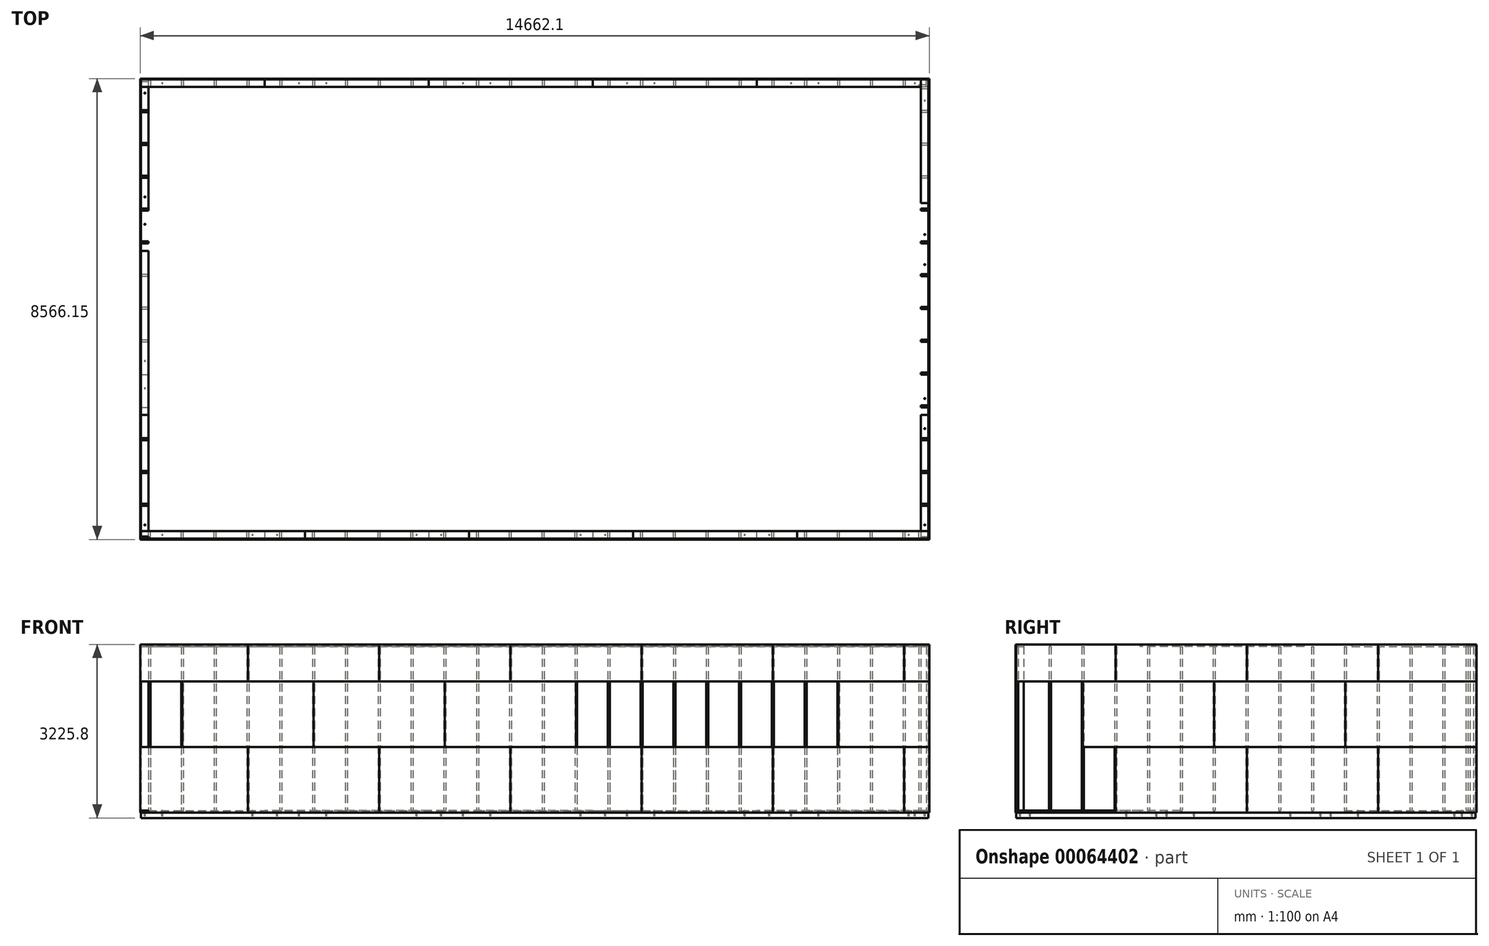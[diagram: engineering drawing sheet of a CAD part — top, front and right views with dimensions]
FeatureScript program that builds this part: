
annotation { "Feature Type Name" : "Feature", "Feature Type Description" : "" }
export const myFeature = defineFeature(function(context is Context, id is Id, definition is map)
    precondition{}
    {
        {
            var Q0;
            Q0=qCreatedBy(makeId("Top.planeOp"),FACE);
            var sketch = newSketch(context, id + "F0", { "sketchPlane" : qUnion([Q0])});
            skLineSegment(sketch, "E0.bottom", {"start": v(0, 8534.4) * mm, "end": v(14630.4, 8534.4) * mm});
            skLineSegment(sketch, "E0.top", {"start": v(0, 0) * mm, "end": v(14630.4, 0) * mm});
            skLineSegment(sketch, "E0.left", {"start": v(0, 8534.4) * mm, "end": v(0, 0) * mm});
            skLineSegment(sketch, "E0.right", {"start": v(14630.4, 8534.4) * mm, "end": v(14630.4, 0) * mm});
            skSolve(sketch);
        }
        {
            var Q0;
            Q0=makeQuery(id+"F0.imprint","IMPRINT",FACE,{"disambiguationData":[TD([[makeQuery(id+"F0.imprint","IMPRINT",EDGE,{"derivedFrom":sQuery(id+"F0.wireOp",EDGE,"E0.bottom")}),-1.0]])]});
            extrude(context, id + "F1", {"entities" : qUnion([Q0]), "oppositeDirection" : true, "depth" : 101.6 * mm});
        }
        {
            var Q0;
            Q0=makeQuery(id+"F1.opExtrude","CAP_FACE",FACE,{"disambiguationData":[OSD([sQuery(id+"F0.wireOp",EDGE,"E0.bottom"),sQuery(id+"F0.wireOp",EDGE,"E0.top"),sQuery(id+"F0.wireOp",EDGE,"E0.left"),sQuery(id+"F0.wireOp",EDGE,"E0.right")])],"isStart":true});
            var sketch = newSketch(context, id + "F2", { "sketchPlane" : qUnion([Q0])});
            skLineSegment(sketch, "E1.bottom", {"start": v(0, 0) * mm, "end": v(139.7, 0) * mm});
            skLineSegment(sketch, "E1.top", {"start": v(0, 3048) * mm, "end": v(139.7, 3048) * mm});
            skLineSegment(sketch, "E1.left", {"start": v(0, 0) * mm, "end": v(0, 3048) * mm});
            skLineSegment(sketch, "E1.right", {"start": v(139.7, 0) * mm, "end": v(139.7, 3048) * mm});
            skLineSegment(sketch, "E2.bottom", {"start": v(139.7, 8534.4) * mm, "end": v(3187.7, 8534.4) * mm});
            skLineSegment(sketch, "E2.top", {"start": v(139.7, 8394.7) * mm, "end": v(3187.7, 8394.7) * mm});
            skLineSegment(sketch, "E2.left", {"start": v(139.7, 8534.4) * mm, "end": v(139.7, 8394.7) * mm});
            skLineSegment(sketch, "E2.right", {"start": v(3187.7, 8534.4) * mm, "end": v(3187.7, 8394.7) * mm});
            skLineSegment(sketch, "E3.bottom", {"start": v(3187.7, 8394.7) * mm, "end": v(6235.7, 8394.7) * mm});
            skLineSegment(sketch, "E3.top", {"start": v(3187.7, 8534.4) * mm, "end": v(6235.7, 8534.4) * mm});
            skLineSegment(sketch, "E3.left", {"start": v(3187.7, 8394.7) * mm, "end": v(3187.7, 8534.4) * mm});
            skLineSegment(sketch, "E3.right", {"start": v(6235.7, 8394.7) * mm, "end": v(6235.7, 8534.4) * mm});
            skLineSegment(sketch, "E4.bottom", {"start": v(6235.7, 8394.7) * mm, "end": v(9283.7, 8394.7) * mm});
            skLineSegment(sketch, "E4.top", {"start": v(6235.7, 8534.4) * mm, "end": v(9283.7, 8534.4) * mm});
            skLineSegment(sketch, "E4.right", {"start": v(9283.7, 8394.7) * mm, "end": v(9283.7, 8534.4) * mm});
            skLineSegment(sketch, "E5.bottom", {"start": v(9283.7, 8394.7) * mm, "end": v(12331.7, 8394.7) * mm});
            skLineSegment(sketch, "E5.top", {"start": v(9283.7, 8534.4) * mm, "end": v(12331.7, 8534.4) * mm});
            skLineSegment(sketch, "E5.right", {"start": v(12331.7, 8394.7) * mm, "end": v(12331.7, 8534.4) * mm});
            skLineSegment(sketch, "E6.bottom", {"start": v(12331.7, 8394.7) * mm, "end": v(14630.4, 8394.7) * mm});
            skLineSegment(sketch, "E6.top", {"start": v(12331.7, 8534.4) * mm, "end": v(14630.4, 8534.4) * mm});
            skLineSegment(sketch, "E6.right", {"start": v(14630.4, 8394.7) * mm, "end": v(14630.4, 8534.4) * mm});
            skLineSegment(sketch, "E7.bottom", {"start": v(139.7, 3048) * mm, "end": v(0, 3048) * mm});
            skLineSegment(sketch, "E7.top", {"start": v(139.7, 6096) * mm, "end": v(0, 6096) * mm});
            skLineSegment(sketch, "E7.left", {"start": v(139.7, 3048) * mm, "end": v(139.7, 6096) * mm});
            skLineSegment(sketch, "E7.right", {"start": v(0, 3048) * mm, "end": v(0, 6096) * mm});
            skLineSegment(sketch, "E8.top", {"start": v(139.7, 8534.4) * mm, "end": v(0, 8534.4) * mm});
            skLineSegment(sketch, "E8.left", {"start": v(139.7, 6096) * mm, "end": v(139.7, 8534.4) * mm});
            skLineSegment(sketch, "E8.right", {"start": v(0, 6096) * mm, "end": v(0, 8534.4) * mm});
            skLineSegment(sketch, "E9.bottom", {"start": v(14630.4, 8394.7) * mm, "end": v(14490.7, 8394.7) * mm});
            skLineSegment(sketch, "E9.top", {"start": v(14630.4, 5346.7) * mm, "end": v(14490.7, 5346.7) * mm});
            skLineSegment(sketch, "E9.left", {"start": v(14630.4, 8394.7) * mm, "end": v(14630.4, 5346.7) * mm});
            skLineSegment(sketch, "E9.right", {"start": v(14490.7, 8394.7) * mm, "end": v(14490.7, 5346.7) * mm});
            skLineSegment(sketch, "E10.bottom", {"start": v(14490.7, 5346.7) * mm, "end": v(14630.4, 5346.7) * mm});
            skLineSegment(sketch, "E10.top", {"start": v(14490.7, 2298.7) * mm, "end": v(14630.4, 2298.7) * mm});
            skLineSegment(sketch, "E10.left", {"start": v(14490.7, 5346.7) * mm, "end": v(14490.7, 2298.7) * mm});
            skLineSegment(sketch, "E10.right", {"start": v(14630.4, 5346.7) * mm, "end": v(14630.4, 2298.7) * mm});
            skLineSegment(sketch, "E11.top", {"start": v(14490.7, 0) * mm, "end": v(14630.4, 0) * mm});
            skLineSegment(sketch, "E11.left", {"start": v(14490.7, 2298.7) * mm, "end": v(14490.7, 0) * mm});
            skLineSegment(sketch, "E11.right", {"start": v(14630.4, 2298.7) * mm, "end": v(14630.4, 0) * mm});
            skLineSegment(sketch, "E12.bottom", {"start": v(14490.7, 0) * mm, "end": v(11442.7, 0) * mm});
            skLineSegment(sketch, "E12.top", {"start": v(14490.7, 139.7) * mm, "end": v(11442.7, 139.7) * mm});
            skLineSegment(sketch, "E12.left", {"start": v(14490.7, 0) * mm, "end": v(14490.7, 139.7) * mm});
            skLineSegment(sketch, "E12.right", {"start": v(11442.7, 0) * mm, "end": v(11442.7, 139.7) * mm});
            skLineSegment(sketch, "E13.bottom", {"start": v(11442.7, 139.7) * mm, "end": v(8394.7, 139.7) * mm});
            skLineSegment(sketch, "E13.top", {"start": v(11442.7, 0) * mm, "end": v(8394.7, 0) * mm});
            skLineSegment(sketch, "E13.left", {"start": v(11442.7, 139.7) * mm, "end": v(11442.7, 0) * mm});
            skLineSegment(sketch, "E13.right", {"start": v(8394.7, 139.7) * mm, "end": v(8394.7, 0) * mm});
            skLineSegment(sketch, "E14.bottom", {"start": v(8394.7, 139.7) * mm, "end": v(5346.7, 139.7) * mm});
            skLineSegment(sketch, "E14.top", {"start": v(8394.7, 0) * mm, "end": v(5346.7, 0) * mm});
            skLineSegment(sketch, "E14.right", {"start": v(5346.7, 139.7) * mm, "end": v(5346.7, 0) * mm});
            skLineSegment(sketch, "E15.bottom", {"start": v(5346.7, 139.7) * mm, "end": v(2298.7, 139.7) * mm});
            skLineSegment(sketch, "E15.top", {"start": v(5346.7, 0) * mm, "end": v(2298.7, 0) * mm});
            skLineSegment(sketch, "E15.right", {"start": v(2298.7, 139.7) * mm, "end": v(2298.7, 0) * mm});
            skLineSegment(sketch, "E16.bottom", {"start": v(2298.7, 139.7) * mm, "end": v(139.7, 139.7) * mm});
            skLineSegment(sketch, "E16.top", {"start": v(2298.7, 0) * mm, "end": v(139.7, 0) * mm});
            skLineSegment(sketch, "E16.right", {"start": v(139.7, 139.7) * mm, "end": v(139.7, 0) * mm});
            skSolve(sketch);
        }
        {
            var Q0;
            Q0=makeQuery(id+"F2.imprint","IMPRINT",FACE,{"disambiguationData":[TD([[makeQuery(id+"F2.imprint","IMPRINT",EDGE,{"derivedFrom":sQuery(id+"F2.wireOp",EDGE,"E1.bottom")}),1.0]])]});
            var Q1;
            {var subQ3=sQuery(id+"F2.wireOp",EDGE,"E7.top");Q1=makeQuery(id+"F2.imprint","IMPRINT",FACE,{"disambiguationData":[TD([[makeQuery(id+"F2.imprint","IMPRINT",EDGE,{"derivedFrom":subQ3}),-1.0]])]});}
            var Q2;
            Q2=makeQuery(id+"F2.imprint","IMPRINT",FACE,{"disambiguationData":[TD([[makeQuery(id+"F2.imprint","IMPRINT",EDGE,{"derivedFrom":sQuery(id+"F2.wireOp",EDGE,"E3.bottom")}),1.0]])]});
            var Q3;
            Q3=makeQuery(id+"F2.imprint","IMPRINT",FACE,{"disambiguationData":[TD([[makeQuery(id+"F2.imprint","IMPRINT",EDGE,{"derivedFrom":sQuery(id+"F2.wireOp",EDGE,"E5.bottom")}),1.0]])]});
            var Q4;
            Q4=makeQuery(id+"F2.imprint","IMPRINT",FACE,{"disambiguationData":[TD([[makeQuery(id+"F2.imprint","IMPRINT",EDGE,{"derivedFrom":sQuery(id+"F2.wireOp",EDGE,"E9.bottom")}),1.0]])]});
            var Q5;
            Q5=makeQuery(id+"F2.imprint","IMPRINT",FACE,{"disambiguationData":[TD([[makeQuery(id+"F2.imprint","IMPRINT",EDGE,{"derivedFrom":sQuery(id+"F2.wireOp",EDGE,"E10.top")}),-1.0]])]});
            var Q6;
            Q6=makeQuery(id+"F2.imprint","IMPRINT",FACE,{"disambiguationData":[TD([[makeQuery(id+"F2.imprint","IMPRINT",EDGE,{"derivedFrom":sQuery(id+"F2.wireOp",EDGE,"E13.bottom")}),1.0]])]});
            var Q7;
            Q7=makeQuery(id+"F2.imprint","IMPRINT",FACE,{"disambiguationData":[TD([[makeQuery(id+"F2.imprint","IMPRINT",EDGE,{"derivedFrom":sQuery(id+"F2.wireOp",EDGE,"E15.bottom")}),1.0]])]});
            extrude(context, id + "F3", {"entities" : qUnion([Q0, Q1, Q2, Q3, Q4, Q5, Q6, Q7]), "depth" : 38.1 * mm});
        }
        {
            var Q0;
            Q0=makeQuery(id+"F2.imprint","IMPRINT",FACE,{"disambiguationData":[TD([[makeQuery(id+"F2.imprint","IMPRINT",EDGE,{"derivedFrom":sQuery(id+"F2.wireOp",EDGE,"E7.bottom")}),-1.0]])]});
            var Q1;
            {var subQ0=sQuery(id+"F2.wireOp",EDGE,"E2.bottom");Q1=makeQuery(id+"F2.imprint","IMPRINT",FACE,{"disambiguationData":[TD([[makeQuery(id+"F2.imprint","IMPRINT",EDGE,{"derivedFrom":subQ0}),-1.0]])]});}
            var Q2;
            Q2=makeQuery(id+"F2.imprint","IMPRINT",FACE,{"disambiguationData":[TD([[makeQuery(id+"F2.imprint","IMPRINT",EDGE,{"derivedFrom":sQuery(id+"F2.wireOp",EDGE,"E4.bottom")}),1.0]])]});
            var Q3;
            Q3=makeQuery(id+"F2.imprint","IMPRINT",FACE,{"disambiguationData":[TD([[makeQuery(id+"F2.imprint","IMPRINT",EDGE,{"derivedFrom":sQuery(id+"F2.wireOp",EDGE,"E6.bottom")}),1.0]])]});
            var Q4;
            Q4=makeQuery(id+"F2.imprint","IMPRINT",FACE,{"disambiguationData":[TD([[makeQuery(id+"F2.imprint","IMPRINT",EDGE,{"derivedFrom":sQuery(id+"F2.wireOp",EDGE,"E10.bottom")}),-1.0]])]});
            var Q5;
            Q5=makeQuery(id+"F2.imprint","IMPRINT",FACE,{"disambiguationData":[TD([[makeQuery(id+"F2.imprint","IMPRINT",EDGE,{"derivedFrom":sQuery(id+"F2.wireOp",EDGE,"E12.bottom")}),1.0]])]});
            var Q6;
            Q6=makeQuery(id+"F2.imprint","IMPRINT",FACE,{"disambiguationData":[TD([[makeQuery(id+"F2.imprint","IMPRINT",EDGE,{"derivedFrom":sQuery(id+"F2.wireOp",EDGE,"E14.bottom")}),1.0]])]});
            var Q7;
            Q7=makeQuery(id+"F2.imprint","IMPRINT",FACE,{"disambiguationData":[TD([[makeQuery(id+"F2.imprint","IMPRINT",EDGE,{"derivedFrom":sQuery(id+"F2.wireOp",EDGE,"E16.bottom")}),1.0]])]});
            extrude(context, id + "F4", {"entities" : qUnion([Q0, Q1, Q2, Q3, Q4, Q5, Q6, Q7]), "depth" : 38.1 * mm});
        }
        {
            var Q0;
            Q0=makeQuery(id+"F3.opExtrude","CAP_FACE",FACE,{"disambiguationData":[OSD([sQuery(id+"F2.wireOp",EDGE,"E1.bottom"),sQuery(id+"F2.wireOp",EDGE,"E1.left"),sQuery(id+"F2.wireOp",EDGE,"E1.right"),sQuery(id+"F2.wireOp",EDGE,"E7.bottom"),sQuery(id+"F2.wireOp",EDGE,"E16.right")])],"isStart":false});
            var sketch = newSketch(context, id + "F5", { "sketchPlane" : qUnion([Q0])});
            skLineSegment(sketch, "E17.bottom", {"start": v(0, 0) * mm, "end": v(139.7, 0) * mm});
            skLineSegment(sketch, "E17.top", {"start": v(0, 38.1) * mm, "end": v(139.7, 38.1) * mm});
            skLineSegment(sketch, "E17.left", {"start": v(0, 0) * mm, "end": v(0, 38.1) * mm});
            skLineSegment(sketch, "E17.right", {"start": v(139.7, 0) * mm, "end": v(139.7, 38.1) * mm});
            skLineSegment(sketch, "E18.bottom", {"start": v(139.7, 38.1) * mm, "end": v(101.6, 38.1) * mm});
            skLineSegment(sketch, "E18.top", {"start": v(139.7, 177.8) * mm, "end": v(101.6, 177.8) * mm});
            skLineSegment(sketch, "E18.left", {"start": v(139.7, 38.1) * mm, "end": v(139.7, 177.8) * mm});
            skLineSegment(sketch, "E18.right", {"start": v(101.6, 38.1) * mm, "end": v(101.6, 177.8) * mm});
            skLineSegment(sketch, "E19.0", {"start": v(2298.7, 139.7) * mm, "end": v(139.7, 139.7) * mm, "construction": true});
            skLineSegment(sketch, "E20.bottom", {"start": v(139.7, 0) * mm, "end": v(177.8, 0) * mm});
            skLineSegment(sketch, "E20.top", {"start": v(139.7, 139.7) * mm, "end": v(177.8, 139.7) * mm});
            skLineSegment(sketch, "E20.left", {"start": v(139.7, 0) * mm, "end": v(139.7, 139.7) * mm});
            skLineSegment(sketch, "E20.right", {"start": v(177.8, 0) * mm, "end": v(177.8, 139.7) * mm});
            skLineSegment(sketch, "E21.1.0.0", {"start": v(749.3, 0) * mm, "end": v(749.3, 139.7) * mm});
            skLineSegment(sketch, "E21.1.0.1", {"start": v(749.3, 139.7) * mm, "end": v(787.4, 139.7) * mm});
            skLineSegment(sketch, "E21.1.0.2", {"start": v(787.4, 0) * mm, "end": v(787.4, 139.7) * mm});
            skLineSegment(sketch, "E21.1.0.3", {"start": v(749.3, 0) * mm, "end": v(787.4, 0) * mm});
            skLineSegment(sketch, "E21.2.0.0", {"start": v(1358.9, 0) * mm, "end": v(1358.9, 139.7) * mm});
            skLineSegment(sketch, "E21.2.0.1", {"start": v(1358.9, 139.7) * mm, "end": v(1397, 139.7) * mm});
            skLineSegment(sketch, "E21.2.0.2", {"start": v(1397, 0) * mm, "end": v(1397, 139.7) * mm});
            skLineSegment(sketch, "E21.2.0.3", {"start": v(1358.9, 0) * mm, "end": v(1397, 0) * mm});
            skLineSegment(sketch, "E21.3.0.0", {"start": v(1968.5, 0) * mm, "end": v(1968.5, 139.7) * mm});
            skLineSegment(sketch, "E21.3.0.1", {"start": v(1968.5, 139.7) * mm, "end": v(2006.6, 139.7) * mm});
            skLineSegment(sketch, "E21.3.0.2", {"start": v(2006.6, 0) * mm, "end": v(2006.6, 139.7) * mm});
            skLineSegment(sketch, "E21.3.0.3", {"start": v(1968.5, 0) * mm, "end": v(2006.6, 0) * mm});
            skLineSegment(sketch, "E21.4.0.0", {"start": v(2578.1, 0) * mm, "end": v(2578.1, 139.7) * mm});
            skLineSegment(sketch, "E21.4.0.1", {"start": v(2578.1, 139.7) * mm, "end": v(2616.2, 139.7) * mm});
            skLineSegment(sketch, "E21.4.0.2", {"start": v(2616.2, 0) * mm, "end": v(2616.2, 139.7) * mm});
            skLineSegment(sketch, "E21.4.0.3", {"start": v(2578.1, 0) * mm, "end": v(2616.2, 0) * mm});
            skLineSegment(sketch, "E21.5.0.0", {"start": v(3187.7, 0) * mm, "end": v(3187.7, 139.7) * mm});
            skLineSegment(sketch, "E21.5.0.1", {"start": v(3187.7, 139.7) * mm, "end": v(3225.8, 139.7) * mm});
            skLineSegment(sketch, "E21.5.0.2", {"start": v(3225.8, 0) * mm, "end": v(3225.8, 139.7) * mm});
            skLineSegment(sketch, "E21.5.0.3", {"start": v(3187.7, 0) * mm, "end": v(3225.8, 0) * mm});
            skLineSegment(sketch, "E21.6.0.0", {"start": v(3797.3, 0) * mm, "end": v(3797.3, 139.7) * mm});
            skLineSegment(sketch, "E21.6.0.1", {"start": v(3797.3, 139.7) * mm, "end": v(3835.4, 139.7) * mm});
            skLineSegment(sketch, "E21.6.0.2", {"start": v(3835.4, 0) * mm, "end": v(3835.4, 139.7) * mm});
            skLineSegment(sketch, "E21.6.0.3", {"start": v(3797.3, 0) * mm, "end": v(3835.4, 0) * mm});
            skLineSegment(sketch, "E21.7.0.0", {"start": v(4406.9, 0) * mm, "end": v(4406.9, 139.7) * mm});
            skLineSegment(sketch, "E21.7.0.1", {"start": v(4406.9, 139.7) * mm, "end": v(4445, 139.7) * mm});
            skLineSegment(sketch, "E21.7.0.2", {"start": v(4445, 0) * mm, "end": v(4445, 139.7) * mm});
            skLineSegment(sketch, "E21.7.0.3", {"start": v(4406.9, 0) * mm, "end": v(4445, 0) * mm});
            skLineSegment(sketch, "E21.8.0.0", {"start": v(5016.5, 0) * mm, "end": v(5016.5, 139.7) * mm});
            skLineSegment(sketch, "E21.8.0.1", {"start": v(5016.5, 139.7) * mm, "end": v(5054.6, 139.7) * mm});
            skLineSegment(sketch, "E21.8.0.2", {"start": v(5054.6, 0) * mm, "end": v(5054.6, 139.7) * mm});
            skLineSegment(sketch, "E21.8.0.3", {"start": v(5016.5, 0) * mm, "end": v(5054.6, 0) * mm});
            skLineSegment(sketch, "E21.9.0.0", {"start": v(5626.1, 0) * mm, "end": v(5626.1, 139.7) * mm});
            skLineSegment(sketch, "E21.9.0.1", {"start": v(5626.1, 139.7) * mm, "end": v(5664.2, 139.7) * mm});
            skLineSegment(sketch, "E21.9.0.2", {"start": v(5664.2, 0) * mm, "end": v(5664.2, 139.7) * mm});
            skLineSegment(sketch, "E21.9.0.3", {"start": v(5626.1, 0) * mm, "end": v(5664.2, 0) * mm});
            skLineSegment(sketch, "E21.10.0.0", {"start": v(6235.7, 0) * mm, "end": v(6235.7, 139.7) * mm});
            skLineSegment(sketch, "E21.10.0.1", {"start": v(6235.7, 139.7) * mm, "end": v(6273.8, 139.7) * mm});
            skLineSegment(sketch, "E21.10.0.2", {"start": v(6273.8, 0) * mm, "end": v(6273.8, 139.7) * mm});
            skLineSegment(sketch, "E21.10.0.3", {"start": v(6235.7, 0) * mm, "end": v(6273.8, 0) * mm});
            skLineSegment(sketch, "E21.11.0.0", {"start": v(6845.3, 0) * mm, "end": v(6845.3, 139.7) * mm});
            skLineSegment(sketch, "E21.11.0.1", {"start": v(6845.3, 139.7) * mm, "end": v(6883.4, 139.7) * mm});
            skLineSegment(sketch, "E21.11.0.2", {"start": v(6883.4, 0) * mm, "end": v(6883.4, 139.7) * mm});
            skLineSegment(sketch, "E21.11.0.3", {"start": v(6845.3, 0) * mm, "end": v(6883.4, 0) * mm});
            skLineSegment(sketch, "E21.12.0.0", {"start": v(7454.9, 0) * mm, "end": v(7454.9, 139.7) * mm});
            skLineSegment(sketch, "E21.12.0.1", {"start": v(7454.9, 139.7) * mm, "end": v(7493, 139.7) * mm});
            skLineSegment(sketch, "E21.12.0.2", {"start": v(7493, 0) * mm, "end": v(7493, 139.7) * mm});
            skLineSegment(sketch, "E21.12.0.3", {"start": v(7454.9, 0) * mm, "end": v(7493, 0) * mm});
            skLineSegment(sketch, "E21.13.0.0", {"start": v(8064.5, 0) * mm, "end": v(8064.5, 139.7) * mm});
            skLineSegment(sketch, "E21.13.0.1", {"start": v(8064.5, 139.7) * mm, "end": v(8102.6, 139.7) * mm});
            skLineSegment(sketch, "E21.13.0.2", {"start": v(8102.6, 0) * mm, "end": v(8102.6, 139.7) * mm});
            skLineSegment(sketch, "E21.13.0.3", {"start": v(8064.5, 0) * mm, "end": v(8102.6, 0) * mm});
            skLineSegment(sketch, "E21.14.0.0", {"start": v(8674.1, 0) * mm, "end": v(8674.1, 139.7) * mm});
            skLineSegment(sketch, "E21.14.0.1", {"start": v(8674.1, 139.7) * mm, "end": v(8712.2, 139.7) * mm});
            skLineSegment(sketch, "E21.14.0.2", {"start": v(8712.2, 0) * mm, "end": v(8712.2, 139.7) * mm});
            skLineSegment(sketch, "E21.14.0.3", {"start": v(8674.1, 0) * mm, "end": v(8712.2, 0) * mm});
            skLineSegment(sketch, "E21.15.0.0", {"start": v(9283.7, 0) * mm, "end": v(9283.7, 139.7) * mm});
            skLineSegment(sketch, "E21.15.0.1", {"start": v(9283.7, 139.7) * mm, "end": v(9321.8, 139.7) * mm});
            skLineSegment(sketch, "E21.15.0.2", {"start": v(9321.8, 0) * mm, "end": v(9321.8, 139.7) * mm});
            skLineSegment(sketch, "E21.15.0.3", {"start": v(9283.7, 0) * mm, "end": v(9321.8, 0) * mm});
            skLineSegment(sketch, "E21.16.0.0", {"start": v(9893.3, 0) * mm, "end": v(9893.3, 139.7) * mm});
            skLineSegment(sketch, "E21.16.0.1", {"start": v(9893.3, 139.7) * mm, "end": v(9931.4, 139.7) * mm});
            skLineSegment(sketch, "E21.16.0.2", {"start": v(9931.4, 0) * mm, "end": v(9931.4, 139.7) * mm});
            skLineSegment(sketch, "E21.16.0.3", {"start": v(9893.3, 0) * mm, "end": v(9931.4, 0) * mm});
            skLineSegment(sketch, "E21.17.0.0", {"start": v(10502.9, 0) * mm, "end": v(10502.9, 139.7) * mm});
            skLineSegment(sketch, "E21.17.0.1", {"start": v(10502.9, 139.7) * mm, "end": v(10541, 139.7) * mm});
            skLineSegment(sketch, "E21.17.0.2", {"start": v(10541, 0) * mm, "end": v(10541, 139.7) * mm});
            skLineSegment(sketch, "E21.17.0.3", {"start": v(10502.9, 0) * mm, "end": v(10541, 0) * mm});
            skLineSegment(sketch, "E21.18.0.0", {"start": v(11112.5, 0) * mm, "end": v(11112.5, 139.7) * mm});
            skLineSegment(sketch, "E21.18.0.1", {"start": v(11112.5, 139.7) * mm, "end": v(11150.6, 139.7) * mm});
            skLineSegment(sketch, "E21.18.0.2", {"start": v(11150.6, 0) * mm, "end": v(11150.6, 139.7) * mm});
            skLineSegment(sketch, "E21.18.0.3", {"start": v(11112.5, 0) * mm, "end": v(11150.6, 0) * mm});
            skLineSegment(sketch, "E21.19.0.0", {"start": v(11722.1, 0) * mm, "end": v(11722.1, 139.7) * mm});
            skLineSegment(sketch, "E21.19.0.1", {"start": v(11722.1, 139.7) * mm, "end": v(11760.2, 139.7) * mm});
            skLineSegment(sketch, "E21.19.0.2", {"start": v(11760.2, 0) * mm, "end": v(11760.2, 139.7) * mm});
            skLineSegment(sketch, "E21.19.0.3", {"start": v(11722.1, 0) * mm, "end": v(11760.2, 0) * mm});
            skLineSegment(sketch, "E21.20.0.0", {"start": v(12331.7, 0) * mm, "end": v(12331.7, 139.7) * mm});
            skLineSegment(sketch, "E21.20.0.1", {"start": v(12331.7, 139.7) * mm, "end": v(12369.8, 139.7) * mm});
            skLineSegment(sketch, "E21.20.0.2", {"start": v(12369.8, 0) * mm, "end": v(12369.8, 139.7) * mm});
            skLineSegment(sketch, "E21.20.0.3", {"start": v(12331.7, 0) * mm, "end": v(12369.8, 0) * mm});
            skLineSegment(sketch, "E21.21.0.0", {"start": v(12941.3, 0) * mm, "end": v(12941.3, 139.7) * mm});
            skLineSegment(sketch, "E21.21.0.1", {"start": v(12941.3, 139.7) * mm, "end": v(12979.4, 139.7) * mm});
            skLineSegment(sketch, "E21.21.0.2", {"start": v(12979.4, 0) * mm, "end": v(12979.4, 139.7) * mm});
            skLineSegment(sketch, "E21.21.0.3", {"start": v(12941.3, 0) * mm, "end": v(12979.4, 0) * mm});
            skLineSegment(sketch, "E21.22.0.0", {"start": v(13550.9, 0) * mm, "end": v(13550.9, 139.7) * mm});
            skLineSegment(sketch, "E21.22.0.1", {"start": v(13550.9, 139.7) * mm, "end": v(13589, 139.7) * mm});
            skLineSegment(sketch, "E21.22.0.2", {"start": v(13589, 0) * mm, "end": v(13589, 139.7) * mm});
            skLineSegment(sketch, "E21.22.0.3", {"start": v(13550.9, 0) * mm, "end": v(13589, 0) * mm});
            skLineSegment(sketch, "E21.23.0.0", {"start": v(14160.5, 0) * mm, "end": v(14160.5, 139.7) * mm});
            skLineSegment(sketch, "E21.23.0.1", {"start": v(14160.5, 139.7) * mm, "end": v(14198.6, 139.7) * mm});
            skLineSegment(sketch, "E21.23.0.2", {"start": v(14198.6, 0) * mm, "end": v(14198.6, 139.7) * mm});
            skLineSegment(sketch, "E21.23.0.3", {"start": v(14160.5, 0) * mm, "end": v(14198.6, 0) * mm});
            skLineSegment(sketch, "E21.direction1", {"start": v(139.7, 0) * mm, "end": v(749.3, 0) * mm, "construction": true});
            skLineSegment(sketch, "E22.0.1.0", {"start": v(0, 609.6) * mm, "end": v(139.7, 609.6) * mm});
            skLineSegment(sketch, "E22.0.1.1", {"start": v(0, 647.7) * mm, "end": v(139.7, 647.7) * mm});
            skLineSegment(sketch, "E22.0.1.2", {"start": v(0, 609.6) * mm, "end": v(0, 647.7) * mm});
            skLineSegment(sketch, "E22.0.1.3", {"start": v(139.7, 609.6) * mm, "end": v(139.7, 647.7) * mm});
            skLineSegment(sketch, "E22.0.2.0", {"start": v(0, 1219.2) * mm, "end": v(139.7, 1219.2) * mm});
            skLineSegment(sketch, "E22.0.2.1", {"start": v(0, 1257.3) * mm, "end": v(139.7, 1257.3) * mm});
            skLineSegment(sketch, "E22.0.2.2", {"start": v(0, 1219.2) * mm, "end": v(0, 1257.3) * mm});
            skLineSegment(sketch, "E22.0.2.3", {"start": v(139.7, 1219.2) * mm, "end": v(139.7, 1257.3) * mm});
            skLineSegment(sketch, "E22.0.3.0", {"start": v(0, 1828.8) * mm, "end": v(139.7, 1828.8) * mm});
            skLineSegment(sketch, "E22.0.3.1", {"start": v(0, 1866.9) * mm, "end": v(139.7, 1866.9) * mm});
            skLineSegment(sketch, "E22.0.3.2", {"start": v(0, 1828.8) * mm, "end": v(0, 1866.9) * mm});
            skLineSegment(sketch, "E22.0.3.3", {"start": v(139.7, 1828.8) * mm, "end": v(139.7, 1866.9) * mm});
            skLineSegment(sketch, "E22.0.4.0", {"start": v(0, 2438.4) * mm, "end": v(139.7, 2438.4) * mm});
            skLineSegment(sketch, "E22.0.4.1", {"start": v(0, 2476.5) * mm, "end": v(139.7, 2476.5) * mm});
            skLineSegment(sketch, "E22.0.4.2", {"start": v(0, 2438.4) * mm, "end": v(0, 2476.5) * mm});
            skLineSegment(sketch, "E22.0.4.3", {"start": v(139.7, 2438.4) * mm, "end": v(139.7, 2476.5) * mm});
            skLineSegment(sketch, "E22.0.5.0", {"start": v(0, 3048) * mm, "end": v(139.7, 3048) * mm});
            skLineSegment(sketch, "E22.0.5.1", {"start": v(0, 3086.1) * mm, "end": v(139.7, 3086.1) * mm});
            skLineSegment(sketch, "E22.0.5.2", {"start": v(0, 3048) * mm, "end": v(0, 3086.1) * mm});
            skLineSegment(sketch, "E22.0.5.3", {"start": v(139.7, 3048) * mm, "end": v(139.7, 3086.1) * mm});
            skLineSegment(sketch, "E22.0.6.0", {"start": v(0, 3657.6) * mm, "end": v(139.7, 3657.6) * mm});
            skLineSegment(sketch, "E22.0.6.1", {"start": v(0, 3695.7) * mm, "end": v(139.7, 3695.7) * mm});
            skLineSegment(sketch, "E22.0.6.2", {"start": v(0, 3657.6) * mm, "end": v(0, 3695.7) * mm});
            skLineSegment(sketch, "E22.0.6.3", {"start": v(139.7, 3657.6) * mm, "end": v(139.7, 3695.7) * mm});
            skLineSegment(sketch, "E22.0.7.0", {"start": v(0, 4267.2) * mm, "end": v(139.7, 4267.2) * mm});
            skLineSegment(sketch, "E22.0.7.1", {"start": v(0, 4305.3) * mm, "end": v(139.7, 4305.3) * mm});
            skLineSegment(sketch, "E22.0.7.2", {"start": v(0, 4267.2) * mm, "end": v(0, 4305.3) * mm});
            skLineSegment(sketch, "E22.0.7.3", {"start": v(139.7, 4267.2) * mm, "end": v(139.7, 4305.3) * mm});
            skLineSegment(sketch, "E22.0.8.0", {"start": v(0, 4876.8) * mm, "end": v(139.7, 4876.8) * mm});
            skLineSegment(sketch, "E22.0.8.1", {"start": v(0, 4914.9) * mm, "end": v(139.7, 4914.9) * mm});
            skLineSegment(sketch, "E22.0.8.2", {"start": v(0, 4876.8) * mm, "end": v(0, 4914.9) * mm});
            skLineSegment(sketch, "E22.0.8.3", {"start": v(139.7, 4876.8) * mm, "end": v(139.7, 4914.9) * mm});
            skLineSegment(sketch, "E22.0.9.0", {"start": v(0, 5486.4) * mm, "end": v(139.7, 5486.4) * mm});
            skLineSegment(sketch, "E22.0.9.1", {"start": v(0, 5524.5) * mm, "end": v(139.7, 5524.5) * mm});
            skLineSegment(sketch, "E22.0.9.2", {"start": v(0, 5486.4) * mm, "end": v(0, 5524.5) * mm});
            skLineSegment(sketch, "E22.0.9.3", {"start": v(139.7, 5486.4) * mm, "end": v(139.7, 5524.5) * mm});
            skLineSegment(sketch, "E22.0.10.0", {"start": v(0, 6096) * mm, "end": v(139.7, 6096) * mm});
            skLineSegment(sketch, "E22.0.10.1", {"start": v(0, 6134.1) * mm, "end": v(139.7, 6134.1) * mm});
            skLineSegment(sketch, "E22.0.10.2", {"start": v(0, 6096) * mm, "end": v(0, 6134.1) * mm});
            skLineSegment(sketch, "E22.0.10.3", {"start": v(139.7, 6096) * mm, "end": v(139.7, 6134.1) * mm});
            skLineSegment(sketch, "E22.0.11.0", {"start": v(0, 6705.6) * mm, "end": v(139.7, 6705.6) * mm});
            skLineSegment(sketch, "E22.0.11.1", {"start": v(0, 6743.7) * mm, "end": v(139.7, 6743.7) * mm});
            skLineSegment(sketch, "E22.0.11.2", {"start": v(0, 6705.6) * mm, "end": v(0, 6743.7) * mm});
            skLineSegment(sketch, "E22.0.11.3", {"start": v(139.7, 6705.6) * mm, "end": v(139.7, 6743.7) * mm});
            skLineSegment(sketch, "E22.0.12.0", {"start": v(0, 7315.2) * mm, "end": v(139.7, 7315.2) * mm});
            skLineSegment(sketch, "E22.0.12.1", {"start": v(0, 7353.3) * mm, "end": v(139.7, 7353.3) * mm});
            skLineSegment(sketch, "E22.0.12.2", {"start": v(0, 7315.2) * mm, "end": v(0, 7353.3) * mm});
            skLineSegment(sketch, "E22.0.12.3", {"start": v(139.7, 7315.2) * mm, "end": v(139.7, 7353.3) * mm});
            skLineSegment(sketch, "E22.0.13.0", {"start": v(0, 7924.8) * mm, "end": v(139.7, 7924.8) * mm});
            skLineSegment(sketch, "E22.0.13.1", {"start": v(0, 7962.9) * mm, "end": v(139.7, 7962.9) * mm});
            skLineSegment(sketch, "E22.0.13.2", {"start": v(0, 7924.8) * mm, "end": v(0, 7962.9) * mm});
            skLineSegment(sketch, "E22.0.13.3", {"start": v(139.7, 7924.8) * mm, "end": v(139.7, 7962.9) * mm});
            skLineSegment(sketch, "E22.direction1", {"start": v(0, 0) * mm, "end": v(25.4, 0) * mm, "construction": true});
            skLineSegment(sketch, "E22.direction2", {"start": v(0, 0) * mm, "end": v(0, 609.6) * mm, "construction": true});
            skLineSegment(sketch, "E23.0", {"start": v(139.7, 8534.4) * mm, "end": v(3187.7, 8534.4) * mm, "construction": true});
            skLineSegment(sketch, "E24.0", {"start": v(139.7, 8394.7) * mm, "end": v(3187.7, 8394.7) * mm, "construction": true});
            skLineSegment(sketch, "E25.0", {"start": v(0, 8534.4) * mm, "end": v(0, 6096) * mm, "construction": true});
            skLineSegment(sketch, "E26.bottom", {"start": v(0, 8534.4) * mm, "end": v(139.7, 8534.4) * mm});
            skLineSegment(sketch, "E26.top", {"start": v(0, 8496.3) * mm, "end": v(139.7, 8496.3) * mm});
            skLineSegment(sketch, "E26.left", {"start": v(0, 8534.4) * mm, "end": v(0, 8496.3) * mm});
            skLineSegment(sketch, "E26.right", {"start": v(139.7, 8534.4) * mm, "end": v(139.7, 8496.3) * mm});
            skLineSegment(sketch, "E27.bottom", {"start": v(139.7, 8496.3) * mm, "end": v(101.6, 8496.3) * mm});
            skLineSegment(sketch, "E27.top", {"start": v(139.7, 8356.6) * mm, "end": v(101.6, 8356.6) * mm});
            skLineSegment(sketch, "E27.left", {"start": v(139.7, 8496.3) * mm, "end": v(139.7, 8356.6) * mm});
            skLineSegment(sketch, "E27.right", {"start": v(101.6, 8496.3) * mm, "end": v(101.6, 8356.6) * mm});
            skLineSegment(sketch, "E28.bottom", {"start": v(139.7, 8534.4) * mm, "end": v(177.8, 8534.4) * mm});
            skLineSegment(sketch, "E28.top", {"start": v(139.7, 8394.7) * mm, "end": v(177.8, 8394.7) * mm});
            skLineSegment(sketch, "E28.left", {"start": v(139.7, 8534.4) * mm, "end": v(139.7, 8394.7) * mm});
            skLineSegment(sketch, "E28.right", {"start": v(177.8, 8534.4) * mm, "end": v(177.8, 8394.7) * mm});
            skLineSegment(sketch, "E29.1.0.0", {"start": v(749.3, 8534.4) * mm, "end": v(787.4, 8534.4) * mm});
            skLineSegment(sketch, "E29.1.0.1", {"start": v(749.3, 8534.4) * mm, "end": v(749.3, 8394.7) * mm});
            skLineSegment(sketch, "E29.1.0.2", {"start": v(787.4, 8534.4) * mm, "end": v(787.4, 8394.7) * mm});
            skLineSegment(sketch, "E29.1.0.3", {"start": v(749.3, 8394.7) * mm, "end": v(787.4, 8394.7) * mm});
            skLineSegment(sketch, "E29.2.0.0", {"start": v(1358.9, 8534.4) * mm, "end": v(1397, 8534.4) * mm});
            skLineSegment(sketch, "E29.2.0.1", {"start": v(1358.9, 8534.4) * mm, "end": v(1358.9, 8394.7) * mm});
            skLineSegment(sketch, "E29.2.0.2", {"start": v(1397, 8534.4) * mm, "end": v(1397, 8394.7) * mm});
            skLineSegment(sketch, "E29.2.0.3", {"start": v(1358.9, 8394.7) * mm, "end": v(1397, 8394.7) * mm});
            skLineSegment(sketch, "E29.3.0.0", {"start": v(1968.5, 8534.4) * mm, "end": v(2006.6, 8534.4) * mm});
            skLineSegment(sketch, "E29.3.0.1", {"start": v(1968.5, 8534.4) * mm, "end": v(1968.5, 8394.7) * mm});
            skLineSegment(sketch, "E29.3.0.2", {"start": v(2006.6, 8534.4) * mm, "end": v(2006.6, 8394.7) * mm});
            skLineSegment(sketch, "E29.3.0.3", {"start": v(1968.5, 8394.7) * mm, "end": v(2006.6, 8394.7) * mm});
            skLineSegment(sketch, "E29.4.0.0", {"start": v(2578.1, 8534.4) * mm, "end": v(2616.2, 8534.4) * mm});
            skLineSegment(sketch, "E29.4.0.1", {"start": v(2578.1, 8534.4) * mm, "end": v(2578.1, 8394.7) * mm});
            skLineSegment(sketch, "E29.4.0.2", {"start": v(2616.2, 8534.4) * mm, "end": v(2616.2, 8394.7) * mm});
            skLineSegment(sketch, "E29.4.0.3", {"start": v(2578.1, 8394.7) * mm, "end": v(2616.2, 8394.7) * mm});
            skLineSegment(sketch, "E29.5.0.0", {"start": v(3187.7, 8534.4) * mm, "end": v(3225.8, 8534.4) * mm});
            skLineSegment(sketch, "E29.5.0.1", {"start": v(3187.7, 8534.4) * mm, "end": v(3187.7, 8394.7) * mm});
            skLineSegment(sketch, "E29.5.0.2", {"start": v(3225.8, 8534.4) * mm, "end": v(3225.8, 8394.7) * mm});
            skLineSegment(sketch, "E29.5.0.3", {"start": v(3187.7, 8394.7) * mm, "end": v(3225.8, 8394.7) * mm});
            skLineSegment(sketch, "E29.6.0.0", {"start": v(3797.3, 8534.4) * mm, "end": v(3835.4, 8534.4) * mm});
            skLineSegment(sketch, "E29.6.0.1", {"start": v(3797.3, 8534.4) * mm, "end": v(3797.3, 8394.7) * mm});
            skLineSegment(sketch, "E29.6.0.2", {"start": v(3835.4, 8534.4) * mm, "end": v(3835.4, 8394.7) * mm});
            skLineSegment(sketch, "E29.6.0.3", {"start": v(3797.3, 8394.7) * mm, "end": v(3835.4, 8394.7) * mm});
            skLineSegment(sketch, "E29.7.0.0", {"start": v(4406.9, 8534.4) * mm, "end": v(4445, 8534.4) * mm});
            skLineSegment(sketch, "E29.7.0.1", {"start": v(4406.9, 8534.4) * mm, "end": v(4406.9, 8394.7) * mm});
            skLineSegment(sketch, "E29.7.0.2", {"start": v(4445, 8534.4) * mm, "end": v(4445, 8394.7) * mm});
            skLineSegment(sketch, "E29.7.0.3", {"start": v(4406.9, 8394.7) * mm, "end": v(4445, 8394.7) * mm});
            skLineSegment(sketch, "E29.8.0.0", {"start": v(5016.5, 8534.4) * mm, "end": v(5054.6, 8534.4) * mm});
            skLineSegment(sketch, "E29.8.0.1", {"start": v(5016.5, 8534.4) * mm, "end": v(5016.5, 8394.7) * mm});
            skLineSegment(sketch, "E29.8.0.2", {"start": v(5054.6, 8534.4) * mm, "end": v(5054.6, 8394.7) * mm});
            skLineSegment(sketch, "E29.8.0.3", {"start": v(5016.5, 8394.7) * mm, "end": v(5054.6, 8394.7) * mm});
            skLineSegment(sketch, "E29.9.0.0", {"start": v(5626.1, 8534.4) * mm, "end": v(5664.2, 8534.4) * mm});
            skLineSegment(sketch, "E29.9.0.1", {"start": v(5626.1, 8534.4) * mm, "end": v(5626.1, 8394.7) * mm});
            skLineSegment(sketch, "E29.9.0.2", {"start": v(5664.2, 8534.4) * mm, "end": v(5664.2, 8394.7) * mm});
            skLineSegment(sketch, "E29.9.0.3", {"start": v(5626.1, 8394.7) * mm, "end": v(5664.2, 8394.7) * mm});
            skLineSegment(sketch, "E29.10.0.0", {"start": v(6235.7, 8534.4) * mm, "end": v(6273.8, 8534.4) * mm});
            skLineSegment(sketch, "E29.10.0.1", {"start": v(6235.7, 8534.4) * mm, "end": v(6235.7, 8394.7) * mm});
            skLineSegment(sketch, "E29.10.0.2", {"start": v(6273.8, 8534.4) * mm, "end": v(6273.8, 8394.7) * mm});
            skLineSegment(sketch, "E29.10.0.3", {"start": v(6235.7, 8394.7) * mm, "end": v(6273.8, 8394.7) * mm});
            skLineSegment(sketch, "E29.11.0.0", {"start": v(6845.3, 8534.4) * mm, "end": v(6883.4, 8534.4) * mm});
            skLineSegment(sketch, "E29.11.0.1", {"start": v(6845.3, 8534.4) * mm, "end": v(6845.3, 8394.7) * mm});
            skLineSegment(sketch, "E29.11.0.2", {"start": v(6883.4, 8534.4) * mm, "end": v(6883.4, 8394.7) * mm});
            skLineSegment(sketch, "E29.11.0.3", {"start": v(6845.3, 8394.7) * mm, "end": v(6883.4, 8394.7) * mm});
            skLineSegment(sketch, "E29.12.0.0", {"start": v(7454.9, 8534.4) * mm, "end": v(7493, 8534.4) * mm});
            skLineSegment(sketch, "E29.12.0.1", {"start": v(7454.9, 8534.4) * mm, "end": v(7454.9, 8394.7) * mm});
            skLineSegment(sketch, "E29.12.0.2", {"start": v(7493, 8534.4) * mm, "end": v(7493, 8394.7) * mm});
            skLineSegment(sketch, "E29.12.0.3", {"start": v(7454.9, 8394.7) * mm, "end": v(7493, 8394.7) * mm});
            skLineSegment(sketch, "E29.13.0.0", {"start": v(8064.5, 8534.4) * mm, "end": v(8102.6, 8534.4) * mm});
            skLineSegment(sketch, "E29.13.0.1", {"start": v(8064.5, 8534.4) * mm, "end": v(8064.5, 8394.7) * mm});
            skLineSegment(sketch, "E29.13.0.2", {"start": v(8102.6, 8534.4) * mm, "end": v(8102.6, 8394.7) * mm});
            skLineSegment(sketch, "E29.13.0.3", {"start": v(8064.5, 8394.7) * mm, "end": v(8102.6, 8394.7) * mm});
            skLineSegment(sketch, "E29.14.0.0", {"start": v(8674.1, 8534.4) * mm, "end": v(8712.2, 8534.4) * mm});
            skLineSegment(sketch, "E29.14.0.1", {"start": v(8674.1, 8534.4) * mm, "end": v(8674.1, 8394.7) * mm});
            skLineSegment(sketch, "E29.14.0.2", {"start": v(8712.2, 8534.4) * mm, "end": v(8712.2, 8394.7) * mm});
            skLineSegment(sketch, "E29.14.0.3", {"start": v(8674.1, 8394.7) * mm, "end": v(8712.2, 8394.7) * mm});
            skLineSegment(sketch, "E29.15.0.0", {"start": v(9283.7, 8534.4) * mm, "end": v(9321.8, 8534.4) * mm});
            skLineSegment(sketch, "E29.15.0.1", {"start": v(9283.7, 8534.4) * mm, "end": v(9283.7, 8394.7) * mm});
            skLineSegment(sketch, "E29.15.0.2", {"start": v(9321.8, 8534.4) * mm, "end": v(9321.8, 8394.7) * mm});
            skLineSegment(sketch, "E29.15.0.3", {"start": v(9283.7, 8394.7) * mm, "end": v(9321.8, 8394.7) * mm});
            skLineSegment(sketch, "E29.16.0.0", {"start": v(9893.3, 8534.4) * mm, "end": v(9931.4, 8534.4) * mm});
            skLineSegment(sketch, "E29.16.0.1", {"start": v(9893.3, 8534.4) * mm, "end": v(9893.3, 8394.7) * mm});
            skLineSegment(sketch, "E29.16.0.2", {"start": v(9931.4, 8534.4) * mm, "end": v(9931.4, 8394.7) * mm});
            skLineSegment(sketch, "E29.16.0.3", {"start": v(9893.3, 8394.7) * mm, "end": v(9931.4, 8394.7) * mm});
            skLineSegment(sketch, "E29.17.0.0", {"start": v(10502.9, 8534.4) * mm, "end": v(10541, 8534.4) * mm});
            skLineSegment(sketch, "E29.17.0.1", {"start": v(10502.9, 8534.4) * mm, "end": v(10502.9, 8394.7) * mm});
            skLineSegment(sketch, "E29.17.0.2", {"start": v(10541, 8534.4) * mm, "end": v(10541, 8394.7) * mm});
            skLineSegment(sketch, "E29.17.0.3", {"start": v(10502.9, 8394.7) * mm, "end": v(10541, 8394.7) * mm});
            skLineSegment(sketch, "E29.18.0.0", {"start": v(11112.5, 8534.4) * mm, "end": v(11150.6, 8534.4) * mm});
            skLineSegment(sketch, "E29.18.0.1", {"start": v(11112.5, 8534.4) * mm, "end": v(11112.5, 8394.7) * mm});
            skLineSegment(sketch, "E29.18.0.2", {"start": v(11150.6, 8534.4) * mm, "end": v(11150.6, 8394.7) * mm});
            skLineSegment(sketch, "E29.18.0.3", {"start": v(11112.5, 8394.7) * mm, "end": v(11150.6, 8394.7) * mm});
            skLineSegment(sketch, "E29.19.0.0", {"start": v(11722.1, 8534.4) * mm, "end": v(11760.2, 8534.4) * mm});
            skLineSegment(sketch, "E29.19.0.1", {"start": v(11722.1, 8534.4) * mm, "end": v(11722.1, 8394.7) * mm});
            skLineSegment(sketch, "E29.19.0.2", {"start": v(11760.2, 8534.4) * mm, "end": v(11760.2, 8394.7) * mm});
            skLineSegment(sketch, "E29.19.0.3", {"start": v(11722.1, 8394.7) * mm, "end": v(11760.2, 8394.7) * mm});
            skLineSegment(sketch, "E29.20.0.0", {"start": v(12331.7, 8534.4) * mm, "end": v(12369.8, 8534.4) * mm});
            skLineSegment(sketch, "E29.20.0.1", {"start": v(12331.7, 8534.4) * mm, "end": v(12331.7, 8394.7) * mm});
            skLineSegment(sketch, "E29.20.0.2", {"start": v(12369.8, 8534.4) * mm, "end": v(12369.8, 8394.7) * mm});
            skLineSegment(sketch, "E29.20.0.3", {"start": v(12331.7, 8394.7) * mm, "end": v(12369.8, 8394.7) * mm});
            skLineSegment(sketch, "E29.21.0.0", {"start": v(12941.3, 8534.4) * mm, "end": v(12979.4, 8534.4) * mm});
            skLineSegment(sketch, "E29.21.0.1", {"start": v(12941.3, 8534.4) * mm, "end": v(12941.3, 8394.7) * mm});
            skLineSegment(sketch, "E29.21.0.2", {"start": v(12979.4, 8534.4) * mm, "end": v(12979.4, 8394.7) * mm});
            skLineSegment(sketch, "E29.21.0.3", {"start": v(12941.3, 8394.7) * mm, "end": v(12979.4, 8394.7) * mm});
            skLineSegment(sketch, "E29.22.0.0", {"start": v(13550.9, 8534.4) * mm, "end": v(13589, 8534.4) * mm});
            skLineSegment(sketch, "E29.22.0.1", {"start": v(13550.9, 8534.4) * mm, "end": v(13550.9, 8394.7) * mm});
            skLineSegment(sketch, "E29.22.0.2", {"start": v(13589, 8534.4) * mm, "end": v(13589, 8394.7) * mm});
            skLineSegment(sketch, "E29.22.0.3", {"start": v(13550.9, 8394.7) * mm, "end": v(13589, 8394.7) * mm});
            skLineSegment(sketch, "E29.23.0.0", {"start": v(14160.5, 8534.4) * mm, "end": v(14198.6, 8534.4) * mm});
            skLineSegment(sketch, "E29.23.0.1", {"start": v(14160.5, 8534.4) * mm, "end": v(14160.5, 8394.7) * mm});
            skLineSegment(sketch, "E29.23.0.2", {"start": v(14198.6, 8534.4) * mm, "end": v(14198.6, 8394.7) * mm});
            skLineSegment(sketch, "E29.23.0.3", {"start": v(14160.5, 8394.7) * mm, "end": v(14198.6, 8394.7) * mm});
            skLineSegment(sketch, "E29.direction1", {"start": v(139.7, 8534.4) * mm, "end": v(749.3, 8534.4) * mm, "construction": true});
            skLineSegment(sketch, "E30.0", {"start": v(14490.7, 0) * mm, "end": v(14630.4, 0) * mm, "construction": true});
            skLineSegment(sketch, "E31.bottom", {"start": v(14490.7, 0) * mm, "end": v(14452.6, 0) * mm});
            skLineSegment(sketch, "E31.top", {"start": v(14490.7, 139.7) * mm, "end": v(14452.6, 139.7) * mm});
            skLineSegment(sketch, "E31.left", {"start": v(14490.7, 0) * mm, "end": v(14490.7, 139.7) * mm});
            skLineSegment(sketch, "E31.right", {"start": v(14452.6, 0) * mm, "end": v(14452.6, 139.7) * mm});
            skLineSegment(sketch, "E32.bottom", {"start": v(14490.7, 0) * mm, "end": v(14630.4, 0) * mm});
            skLineSegment(sketch, "E32.top", {"start": v(14490.7, 38.1) * mm, "end": v(14630.4, 38.1) * mm});
            skLineSegment(sketch, "E32.left", {"start": v(14490.7, 0) * mm, "end": v(14490.7, 38.1) * mm});
            skLineSegment(sketch, "E32.right", {"start": v(14630.4, 0) * mm, "end": v(14630.4, 38.1) * mm});
            skLineSegment(sketch, "E33.bottom", {"start": v(14490.7, 38.1) * mm, "end": v(14528.8, 38.1) * mm});
            skLineSegment(sketch, "E33.top", {"start": v(14490.7, 177.8) * mm, "end": v(14528.8, 177.8) * mm});
            skLineSegment(sketch, "E33.left", {"start": v(14490.7, 38.1) * mm, "end": v(14490.7, 177.8) * mm});
            skLineSegment(sketch, "E33.right", {"start": v(14528.8, 38.1) * mm, "end": v(14528.8, 177.8) * mm});
            skLineSegment(sketch, "E34.0.1.0", {"start": v(14490.7, 609.6) * mm, "end": v(14630.4, 609.6) * mm});
            skLineSegment(sketch, "E34.0.1.1", {"start": v(14490.7, 647.7) * mm, "end": v(14630.4, 647.7) * mm});
            skLineSegment(sketch, "E34.0.1.2", {"start": v(14630.4, 609.6) * mm, "end": v(14630.4, 647.7) * mm});
            skLineSegment(sketch, "E34.0.1.3", {"start": v(14490.7, 609.6) * mm, "end": v(14490.7, 647.7) * mm});
            skLineSegment(sketch, "E34.0.2.0", {"start": v(14490.7, 1219.2) * mm, "end": v(14630.4, 1219.2) * mm});
            skLineSegment(sketch, "E34.0.2.1", {"start": v(14490.7, 1257.3) * mm, "end": v(14630.4, 1257.3) * mm});
            skLineSegment(sketch, "E34.0.2.2", {"start": v(14630.4, 1219.2) * mm, "end": v(14630.4, 1257.3) * mm});
            skLineSegment(sketch, "E34.0.2.3", {"start": v(14490.7, 1219.2) * mm, "end": v(14490.7, 1257.3) * mm});
            skLineSegment(sketch, "E34.0.3.0", {"start": v(14490.7, 1828.8) * mm, "end": v(14630.4, 1828.8) * mm});
            skLineSegment(sketch, "E34.0.3.1", {"start": v(14490.7, 1866.9) * mm, "end": v(14630.4, 1866.9) * mm});
            skLineSegment(sketch, "E34.0.3.2", {"start": v(14630.4, 1828.8) * mm, "end": v(14630.4, 1866.9) * mm});
            skLineSegment(sketch, "E34.0.3.3", {"start": v(14490.7, 1828.8) * mm, "end": v(14490.7, 1866.9) * mm});
            skLineSegment(sketch, "E34.0.4.0", {"start": v(14490.7, 2438.4) * mm, "end": v(14630.4, 2438.4) * mm});
            skLineSegment(sketch, "E34.0.4.1", {"start": v(14490.7, 2476.5) * mm, "end": v(14630.4, 2476.5) * mm});
            skLineSegment(sketch, "E34.0.4.2", {"start": v(14630.4, 2438.4) * mm, "end": v(14630.4, 2476.5) * mm});
            skLineSegment(sketch, "E34.0.4.3", {"start": v(14490.7, 2438.4) * mm, "end": v(14490.7, 2476.5) * mm});
            skLineSegment(sketch, "E34.0.5.0", {"start": v(14490.7, 3048) * mm, "end": v(14630.4, 3048) * mm});
            skLineSegment(sketch, "E34.0.5.1", {"start": v(14490.7, 3086.1) * mm, "end": v(14630.4, 3086.1) * mm});
            skLineSegment(sketch, "E34.0.5.2", {"start": v(14630.4, 3048) * mm, "end": v(14630.4, 3086.1) * mm});
            skLineSegment(sketch, "E34.0.5.3", {"start": v(14490.7, 3048) * mm, "end": v(14490.7, 3086.1) * mm});
            skLineSegment(sketch, "E34.0.6.0", {"start": v(14490.7, 3657.6) * mm, "end": v(14630.4, 3657.6) * mm});
            skLineSegment(sketch, "E34.0.6.1", {"start": v(14490.7, 3695.7) * mm, "end": v(14630.4, 3695.7) * mm});
            skLineSegment(sketch, "E34.0.6.2", {"start": v(14630.4, 3657.6) * mm, "end": v(14630.4, 3695.7) * mm});
            skLineSegment(sketch, "E34.0.6.3", {"start": v(14490.7, 3657.6) * mm, "end": v(14490.7, 3695.7) * mm});
            skLineSegment(sketch, "E34.0.7.0", {"start": v(14490.7, 4267.2) * mm, "end": v(14630.4, 4267.2) * mm});
            skLineSegment(sketch, "E34.0.7.1", {"start": v(14490.7, 4305.3) * mm, "end": v(14630.4, 4305.3) * mm});
            skLineSegment(sketch, "E34.0.7.2", {"start": v(14630.4, 4267.2) * mm, "end": v(14630.4, 4305.3) * mm});
            skLineSegment(sketch, "E34.0.7.3", {"start": v(14490.7, 4267.2) * mm, "end": v(14490.7, 4305.3) * mm});
            skLineSegment(sketch, "E34.0.8.0", {"start": v(14490.7, 4876.8) * mm, "end": v(14630.4, 4876.8) * mm});
            skLineSegment(sketch, "E34.0.8.1", {"start": v(14490.7, 4914.9) * mm, "end": v(14630.4, 4914.9) * mm});
            skLineSegment(sketch, "E34.0.8.2", {"start": v(14630.4, 4876.8) * mm, "end": v(14630.4, 4914.9) * mm});
            skLineSegment(sketch, "E34.0.8.3", {"start": v(14490.7, 4876.8) * mm, "end": v(14490.7, 4914.9) * mm});
            skLineSegment(sketch, "E34.0.9.0", {"start": v(14490.7, 5486.4) * mm, "end": v(14630.4, 5486.4) * mm});
            skLineSegment(sketch, "E34.0.9.1", {"start": v(14490.7, 5524.5) * mm, "end": v(14630.4, 5524.5) * mm});
            skLineSegment(sketch, "E34.0.9.2", {"start": v(14630.4, 5486.4) * mm, "end": v(14630.4, 5524.5) * mm});
            skLineSegment(sketch, "E34.0.9.3", {"start": v(14490.7, 5486.4) * mm, "end": v(14490.7, 5524.5) * mm});
            skLineSegment(sketch, "E34.0.10.0", {"start": v(14490.7, 6096) * mm, "end": v(14630.4, 6096) * mm});
            skLineSegment(sketch, "E34.0.10.1", {"start": v(14490.7, 6134.1) * mm, "end": v(14630.4, 6134.1) * mm});
            skLineSegment(sketch, "E34.0.10.2", {"start": v(14630.4, 6096) * mm, "end": v(14630.4, 6134.1) * mm});
            skLineSegment(sketch, "E34.0.10.3", {"start": v(14490.7, 6096) * mm, "end": v(14490.7, 6134.1) * mm});
            skLineSegment(sketch, "E34.0.11.0", {"start": v(14490.7, 6705.6) * mm, "end": v(14630.4, 6705.6) * mm});
            skLineSegment(sketch, "E34.0.11.1", {"start": v(14490.7, 6743.7) * mm, "end": v(14630.4, 6743.7) * mm});
            skLineSegment(sketch, "E34.0.11.2", {"start": v(14630.4, 6705.6) * mm, "end": v(14630.4, 6743.7) * mm});
            skLineSegment(sketch, "E34.0.11.3", {"start": v(14490.7, 6705.6) * mm, "end": v(14490.7, 6743.7) * mm});
            skLineSegment(sketch, "E34.0.12.0", {"start": v(14490.7, 7315.2) * mm, "end": v(14630.4, 7315.2) * mm});
            skLineSegment(sketch, "E34.0.12.1", {"start": v(14490.7, 7353.3) * mm, "end": v(14630.4, 7353.3) * mm});
            skLineSegment(sketch, "E34.0.12.2", {"start": v(14630.4, 7315.2) * mm, "end": v(14630.4, 7353.3) * mm});
            skLineSegment(sketch, "E34.0.12.3", {"start": v(14490.7, 7315.2) * mm, "end": v(14490.7, 7353.3) * mm});
            skLineSegment(sketch, "E34.0.13.0", {"start": v(14490.7, 7924.8) * mm, "end": v(14630.4, 7924.8) * mm});
            skLineSegment(sketch, "E34.0.13.1", {"start": v(14490.7, 7962.9) * mm, "end": v(14630.4, 7962.9) * mm});
            skLineSegment(sketch, "E34.0.13.2", {"start": v(14630.4, 7924.8) * mm, "end": v(14630.4, 7962.9) * mm});
            skLineSegment(sketch, "E34.0.13.3", {"start": v(14490.7, 7924.8) * mm, "end": v(14490.7, 7962.9) * mm});
            skLineSegment(sketch, "E34.direction1", {"start": v(14490.7, 0) * mm, "end": v(14516.1, 0) * mm, "construction": true});
            skLineSegment(sketch, "E34.direction2", {"start": v(14490.7, 0) * mm, "end": v(14490.7, 609.6) * mm, "construction": true});
            skLineSegment(sketch, "E35.bottom", {"start": v(14630.4, 8394.7) * mm, "end": v(14592.3, 8394.7) * mm});
            skLineSegment(sketch, "E35.top", {"start": v(14630.4, 8534.4) * mm, "end": v(14592.3, 8534.4) * mm});
            skLineSegment(sketch, "E35.left", {"start": v(14630.4, 8394.7) * mm, "end": v(14630.4, 8534.4) * mm});
            skLineSegment(sketch, "E35.right", {"start": v(14592.3, 8394.7) * mm, "end": v(14592.3, 8534.4) * mm});
            skLineSegment(sketch, "E36.bottom", {"start": v(14592.3, 8394.7) * mm, "end": v(14452.6, 8394.7) * mm});
            skLineSegment(sketch, "E36.top", {"start": v(14592.3, 8432.8) * mm, "end": v(14452.6, 8432.8) * mm});
            skLineSegment(sketch, "E36.left", {"start": v(14592.3, 8394.7) * mm, "end": v(14592.3, 8432.8) * mm});
            skLineSegment(sketch, "E36.right", {"start": v(14452.6, 8394.7) * mm, "end": v(14452.6, 8432.8) * mm});
            skLineSegment(sketch, "E37.bottom", {"start": v(14630.4, 8394.7) * mm, "end": v(14490.7, 8394.7) * mm});
            skLineSegment(sketch, "E37.top", {"start": v(14630.4, 8356.6) * mm, "end": v(14490.7, 8356.6) * mm});
            skLineSegment(sketch, "E37.left", {"start": v(14630.4, 8394.7) * mm, "end": v(14630.4, 8356.6) * mm});
            skLineSegment(sketch, "E37.right", {"start": v(14490.7, 8394.7) * mm, "end": v(14490.7, 8356.6) * mm});
            skSolve(sketch);
        }
        {
            var Q0;
            {var subQ1=sQuery(id+"F5.wireOp",EDGE,"E17.bottom");Q0=makeQuery(id+"F5.imprint","IMPRINT",FACE,{"disambiguationData":[TD([[makeQuery(id+"F5.imprint","IMPRINT",EDGE,{"derivedFrom":subQ1}),1.0]])]});}
            var Q1;
            Q1=makeQuery(id+"F5.imprint","IMPRINT",FACE,{"disambiguationData":[TD([[makeQuery(id+"F5.imprint","IMPRINT",EDGE,{"derivedFrom":sQuery(id+"F5.wireOp",EDGE,"E21.1.0.0")}),-1.0]])]});
            var Q2;
            Q2=makeQuery(id+"F5.imprint","IMPRINT",FACE,{"disambiguationData":[TD([[makeQuery(id+"F5.imprint","IMPRINT",EDGE,{"derivedFrom":sQuery(id+"F5.wireOp",EDGE,"E22.0.1.0")}),1.0]])]});
            var Q3;
            Q3=makeQuery(id+"F5.imprint","IMPRINT",FACE,{"disambiguationData":[TD([[makeQuery(id+"F5.imprint","IMPRINT",EDGE,{"derivedFrom":sQuery(id+"F5.wireOp",EDGE,"E21.2.0.0")}),-1.0]])]});
            var Q4;
            Q4=makeQuery(id+"F5.imprint","IMPRINT",FACE,{"disambiguationData":[TD([[makeQuery(id+"F5.imprint","IMPRINT",EDGE,{"derivedFrom":sQuery(id+"F5.wireOp",EDGE,"E22.0.2.0")}),1.0]])]});
            var Q5;
            Q5=makeQuery(id+"F5.imprint","IMPRINT",FACE,{"disambiguationData":[TD([[makeQuery(id+"F5.imprint","IMPRINT",EDGE,{"derivedFrom":sQuery(id+"F5.wireOp",EDGE,"E21.3.0.0")}),-1.0]])]});
            var Q6;
            Q6=makeQuery(id+"F5.imprint","IMPRINT",FACE,{"disambiguationData":[TD([[makeQuery(id+"F5.imprint","IMPRINT",EDGE,{"derivedFrom":sQuery(id+"F5.wireOp",EDGE,"E21.4.0.0")}),-1.0]])]});
            var Q7;
            Q7=makeQuery(id+"F5.imprint","IMPRINT",FACE,{"disambiguationData":[TD([[makeQuery(id+"F5.imprint","IMPRINT",EDGE,{"derivedFrom":sQuery(id+"F5.wireOp",EDGE,"E22.0.3.0")}),1.0]])]});
            var Q8;
            Q8=makeQuery(id+"F5.imprint","IMPRINT",FACE,{"disambiguationData":[TD([[makeQuery(id+"F5.imprint","IMPRINT",EDGE,{"derivedFrom":sQuery(id+"F5.wireOp",EDGE,"E22.0.4.0")}),1.0]])]});
            var Q9;
            Q9=makeQuery(id+"F5.imprint","IMPRINT",FACE,{"disambiguationData":[TD([[makeQuery(id+"F5.imprint","IMPRINT",EDGE,{"derivedFrom":sQuery(id+"F5.wireOp",EDGE,"E22.0.5.0")}),-1.0]])]});
            var Q10;
            Q10=makeQuery(id+"F5.imprint","IMPRINT",FACE,{"disambiguationData":[TD([[makeQuery(id+"F5.imprint","IMPRINT",EDGE,{"derivedFrom":sQuery(id+"F5.wireOp",EDGE,"E22.0.6.0")}),1.0]])]});
            var Q11;
            Q11=makeQuery(id+"F5.imprint","IMPRINT",FACE,{"disambiguationData":[TD([[makeQuery(id+"F5.imprint","IMPRINT",EDGE,{"derivedFrom":sQuery(id+"F5.wireOp",EDGE,"E22.0.7.0")}),1.0]])]});
            var Q12;
            Q12=makeQuery(id+"F5.imprint","IMPRINT",FACE,{"disambiguationData":[TD([[makeQuery(id+"F5.imprint","IMPRINT",EDGE,{"derivedFrom":sQuery(id+"F5.wireOp",EDGE,"E22.0.8.0")}),1.0]])]});
            var Q13;
            Q13=makeQuery(id+"F5.imprint","IMPRINT",FACE,{"disambiguationData":[TD([[makeQuery(id+"F5.imprint","IMPRINT",EDGE,{"derivedFrom":sQuery(id+"F5.wireOp",EDGE,"E22.0.9.0")}),1.0]])]});
            var Q14;
            Q14=makeQuery(id+"F5.imprint","IMPRINT",FACE,{"disambiguationData":[TD([[makeQuery(id+"F5.imprint","IMPRINT",EDGE,{"derivedFrom":sQuery(id+"F5.wireOp",EDGE,"E22.0.10.0")}),1.0]])]});
            var Q15;
            Q15=makeQuery(id+"F5.imprint","IMPRINT",FACE,{"disambiguationData":[TD([[makeQuery(id+"F5.imprint","IMPRINT",EDGE,{"derivedFrom":sQuery(id+"F5.wireOp",EDGE,"E22.0.11.0")}),1.0]])]});
            var Q16;
            Q16=makeQuery(id+"F5.imprint","IMPRINT",FACE,{"disambiguationData":[TD([[makeQuery(id+"F5.imprint","IMPRINT",EDGE,{"derivedFrom":sQuery(id+"F5.wireOp",EDGE,"E22.0.12.0")}),1.0]])]});
            var Q17;
            Q17=makeQuery(id+"F5.imprint","IMPRINT",FACE,{"disambiguationData":[TD([[makeQuery(id+"F5.imprint","IMPRINT",EDGE,{"derivedFrom":sQuery(id+"F5.wireOp",EDGE,"E22.0.13.0")}),1.0]])]});
            var Q18;
            {var subQ2=sQuery(id+"F5.wireOp",EDGE,"E26.bottom");Q18=makeQuery(id+"F5.imprint","IMPRINT",FACE,{"disambiguationData":[TD([[makeQuery(id+"F5.imprint","IMPRINT",EDGE,{"derivedFrom":subQ2}),-1.0]])]});}
            var Q19;
            Q19=makeQuery(id+"F5.imprint","IMPRINT",FACE,{"disambiguationData":[TD([[makeQuery(id+"F5.imprint","IMPRINT",EDGE,{"derivedFrom":sQuery(id+"F5.wireOp",EDGE,"E29.1.0.0")}),-1.0]])]});
            var Q20;
            Q20=makeQuery(id+"F5.imprint","IMPRINT",FACE,{"disambiguationData":[TD([[makeQuery(id+"F5.imprint","IMPRINT",EDGE,{"derivedFrom":sQuery(id+"F5.wireOp",EDGE,"E29.2.0.0")}),-1.0]])]});
            var Q21;
            Q21=makeQuery(id+"F5.imprint","IMPRINT",FACE,{"disambiguationData":[TD([[makeQuery(id+"F5.imprint","IMPRINT",EDGE,{"derivedFrom":sQuery(id+"F5.wireOp",EDGE,"E29.3.0.0")}),-1.0]])]});
            var Q22;
            Q22=makeQuery(id+"F5.imprint","IMPRINT",FACE,{"disambiguationData":[TD([[makeQuery(id+"F5.imprint","IMPRINT",EDGE,{"derivedFrom":sQuery(id+"F5.wireOp",EDGE,"E29.4.0.0")}),-1.0]])]});
            var Q23;
            Q23=makeQuery(id+"F5.imprint","IMPRINT",FACE,{"disambiguationData":[TD([[makeQuery(id+"F5.imprint","IMPRINT",EDGE,{"derivedFrom":sQuery(id+"F5.wireOp",EDGE,"E29.5.0.0")}),-1.0]])]});
            var Q24;
            Q24=makeQuery(id+"F5.imprint","IMPRINT",FACE,{"disambiguationData":[TD([[makeQuery(id+"F5.imprint","IMPRINT",EDGE,{"derivedFrom":sQuery(id+"F5.wireOp",EDGE,"E29.6.0.0")}),-1.0]])]});
            var Q25;
            Q25=makeQuery(id+"F5.imprint","IMPRINT",FACE,{"disambiguationData":[TD([[makeQuery(id+"F5.imprint","IMPRINT",EDGE,{"derivedFrom":sQuery(id+"F5.wireOp",EDGE,"E29.7.0.0")}),-1.0]])]});
            var Q26;
            Q26=makeQuery(id+"F5.imprint","IMPRINT",FACE,{"disambiguationData":[TD([[makeQuery(id+"F5.imprint","IMPRINT",EDGE,{"derivedFrom":sQuery(id+"F5.wireOp",EDGE,"E29.8.0.0")}),-1.0]])]});
            var Q27;
            Q27=makeQuery(id+"F5.imprint","IMPRINT",FACE,{"disambiguationData":[TD([[makeQuery(id+"F5.imprint","IMPRINT",EDGE,{"derivedFrom":sQuery(id+"F5.wireOp",EDGE,"E29.9.0.0")}),-1.0]])]});
            var Q28;
            Q28=makeQuery(id+"F5.imprint","IMPRINT",FACE,{"disambiguationData":[TD([[makeQuery(id+"F5.imprint","IMPRINT",EDGE,{"derivedFrom":sQuery(id+"F5.wireOp",EDGE,"E29.10.0.0")}),-1.0]])]});
            var Q29;
            Q29=makeQuery(id+"F5.imprint","IMPRINT",FACE,{"disambiguationData":[TD([[makeQuery(id+"F5.imprint","IMPRINT",EDGE,{"derivedFrom":sQuery(id+"F5.wireOp",EDGE,"E29.11.0.0")}),-1.0]])]});
            var Q30;
            Q30=makeQuery(id+"F5.imprint","IMPRINT",FACE,{"disambiguationData":[TD([[makeQuery(id+"F5.imprint","IMPRINT",EDGE,{"derivedFrom":sQuery(id+"F5.wireOp",EDGE,"E29.12.0.0")}),-1.0]])]});
            var Q31;
            Q31=makeQuery(id+"F5.imprint","IMPRINT",FACE,{"disambiguationData":[TD([[makeQuery(id+"F5.imprint","IMPRINT",EDGE,{"derivedFrom":sQuery(id+"F5.wireOp",EDGE,"E29.13.0.0")}),-1.0]])]});
            var Q32;
            Q32=makeQuery(id+"F5.imprint","IMPRINT",FACE,{"disambiguationData":[TD([[makeQuery(id+"F5.imprint","IMPRINT",EDGE,{"derivedFrom":sQuery(id+"F5.wireOp",EDGE,"E29.14.0.0")}),-1.0]])]});
            var Q33;
            Q33=makeQuery(id+"F5.imprint","IMPRINT",FACE,{"disambiguationData":[TD([[makeQuery(id+"F5.imprint","IMPRINT",EDGE,{"derivedFrom":sQuery(id+"F5.wireOp",EDGE,"E29.15.0.0")}),-1.0]])]});
            var Q34;
            Q34=makeQuery(id+"F5.imprint","IMPRINT",FACE,{"disambiguationData":[TD([[makeQuery(id+"F5.imprint","IMPRINT",EDGE,{"derivedFrom":sQuery(id+"F5.wireOp",EDGE,"E29.16.0.0")}),-1.0]])]});
            var Q35;
            Q35=makeQuery(id+"F5.imprint","IMPRINT",FACE,{"disambiguationData":[TD([[makeQuery(id+"F5.imprint","IMPRINT",EDGE,{"derivedFrom":sQuery(id+"F5.wireOp",EDGE,"E29.17.0.0")}),-1.0]])]});
            var Q36;
            Q36=makeQuery(id+"F5.imprint","IMPRINT",FACE,{"disambiguationData":[TD([[makeQuery(id+"F5.imprint","IMPRINT",EDGE,{"derivedFrom":sQuery(id+"F5.wireOp",EDGE,"E29.18.0.0")}),-1.0]])]});
            var Q37;
            Q37=makeQuery(id+"F5.imprint","IMPRINT",FACE,{"disambiguationData":[TD([[makeQuery(id+"F5.imprint","IMPRINT",EDGE,{"derivedFrom":sQuery(id+"F5.wireOp",EDGE,"E29.19.0.0")}),-1.0]])]});
            var Q38;
            Q38=makeQuery(id+"F5.imprint","IMPRINT",FACE,{"disambiguationData":[TD([[makeQuery(id+"F5.imprint","IMPRINT",EDGE,{"derivedFrom":sQuery(id+"F5.wireOp",EDGE,"E29.20.0.0")}),-1.0]])]});
            var Q39;
            Q39=makeQuery(id+"F5.imprint","IMPRINT",FACE,{"disambiguationData":[TD([[makeQuery(id+"F5.imprint","IMPRINT",EDGE,{"derivedFrom":sQuery(id+"F5.wireOp",EDGE,"E29.21.0.0")}),-1.0]])]});
            var Q40;
            Q40=makeQuery(id+"F5.imprint","IMPRINT",FACE,{"disambiguationData":[TD([[makeQuery(id+"F5.imprint","IMPRINT",EDGE,{"derivedFrom":sQuery(id+"F5.wireOp",EDGE,"E29.22.0.0")}),-1.0]])]});
            var Q41;
            Q41=makeQuery(id+"F5.imprint","IMPRINT",FACE,{"disambiguationData":[TD([[makeQuery(id+"F5.imprint","IMPRINT",EDGE,{"derivedFrom":sQuery(id+"F5.wireOp",EDGE,"E29.23.0.0")}),-1.0]])]});
            var Q42;
            Q42=makeQuery(id+"F5.imprint","IMPRINT",FACE,{"disambiguationData":[TD([[makeQuery(id+"F5.imprint","IMPRINT",EDGE,{"derivedFrom":sQuery(id+"F5.wireOp",EDGE,"E34.0.13.0")}),1.0]])]});
            var Q43;
            Q43=makeQuery(id+"F5.imprint","IMPRINT",FACE,{"disambiguationData":[TD([[makeQuery(id+"F5.imprint","IMPRINT",EDGE,{"derivedFrom":sQuery(id+"F5.wireOp",EDGE,"E35.top")}),1.0]])]});
            var Q44;
            Q44=makeQuery(id+"F5.imprint","IMPRINT",FACE,{"disambiguationData":[TD([[makeQuery(id+"F5.imprint","IMPRINT",EDGE,{"derivedFrom":sQuery(id+"F5.wireOp",EDGE,"E34.0.12.0")}),1.0]])]});
            var Q45;
            Q45=makeQuery(id+"F5.imprint","IMPRINT",FACE,{"disambiguationData":[TD([[makeQuery(id+"F5.imprint","IMPRINT",EDGE,{"derivedFrom":sQuery(id+"F5.wireOp",EDGE,"E34.0.11.0")}),1.0]])]});
            var Q46;
            Q46=makeQuery(id+"F5.imprint","IMPRINT",FACE,{"disambiguationData":[TD([[makeQuery(id+"F5.imprint","IMPRINT",EDGE,{"derivedFrom":sQuery(id+"F5.wireOp",EDGE,"E34.0.10.0")}),1.0]])]});
            var Q47;
            Q47=makeQuery(id+"F5.imprint","IMPRINT",FACE,{"disambiguationData":[TD([[makeQuery(id+"F5.imprint","IMPRINT",EDGE,{"derivedFrom":sQuery(id+"F5.wireOp",EDGE,"E34.0.9.0")}),1.0]])]});
            var Q48;
            Q48=makeQuery(id+"F5.imprint","IMPRINT",FACE,{"disambiguationData":[TD([[makeQuery(id+"F5.imprint","IMPRINT",EDGE,{"derivedFrom":sQuery(id+"F5.wireOp",EDGE,"E34.0.8.0")}),1.0]])]});
            var Q49;
            Q49=makeQuery(id+"F5.imprint","IMPRINT",FACE,{"disambiguationData":[TD([[makeQuery(id+"F5.imprint","IMPRINT",EDGE,{"derivedFrom":sQuery(id+"F5.wireOp",EDGE,"E34.0.7.0")}),1.0]])]});
            var Q50;
            Q50=makeQuery(id+"F5.imprint","IMPRINT",FACE,{"disambiguationData":[TD([[makeQuery(id+"F5.imprint","IMPRINT",EDGE,{"derivedFrom":sQuery(id+"F5.wireOp",EDGE,"E34.0.6.0")}),1.0]])]});
            var Q51;
            Q51=makeQuery(id+"F5.imprint","IMPRINT",FACE,{"disambiguationData":[TD([[makeQuery(id+"F5.imprint","IMPRINT",EDGE,{"derivedFrom":sQuery(id+"F5.wireOp",EDGE,"E34.0.5.0")}),1.0]])]});
            var Q52;
            Q52=makeQuery(id+"F5.imprint","IMPRINT",FACE,{"disambiguationData":[TD([[makeQuery(id+"F5.imprint","IMPRINT",EDGE,{"derivedFrom":sQuery(id+"F5.wireOp",EDGE,"E34.0.4.0")}),1.0]])]});
            var Q53;
            Q53=makeQuery(id+"F5.imprint","IMPRINT",FACE,{"disambiguationData":[TD([[makeQuery(id+"F5.imprint","IMPRINT",EDGE,{"derivedFrom":sQuery(id+"F5.wireOp",EDGE,"E34.0.3.0")}),1.0]])]});
            var Q54;
            Q54=makeQuery(id+"F5.imprint","IMPRINT",FACE,{"disambiguationData":[TD([[makeQuery(id+"F5.imprint","IMPRINT",EDGE,{"derivedFrom":sQuery(id+"F5.wireOp",EDGE,"E34.0.2.0")}),1.0]])]});
            var Q55;
            Q55=makeQuery(id+"F5.imprint","IMPRINT",FACE,{"disambiguationData":[TD([[makeQuery(id+"F5.imprint","IMPRINT",EDGE,{"derivedFrom":sQuery(id+"F5.wireOp",EDGE,"E34.0.1.0")}),1.0]])]});
            var Q56;
            Q56=makeQuery(id+"F5.imprint","IMPRINT",FACE,{"disambiguationData":[TD([[makeQuery(id+"F5.imprint","IMPRINT",EDGE,{"derivedFrom":sQuery(id+"F5.wireOp",EDGE,"E32.bottom")}),1.0]])]});
            var Q57;
            Q57=makeQuery(id+"F5.imprint","IMPRINT",FACE,{"disambiguationData":[TD([[makeQuery(id+"F5.imprint","IMPRINT",EDGE,{"derivedFrom":sQuery(id+"F5.wireOp",EDGE,"E21.23.0.0")}),-1.0]])]});
            var Q58;
            Q58=makeQuery(id+"F5.imprint","IMPRINT",FACE,{"disambiguationData":[TD([[makeQuery(id+"F5.imprint","IMPRINT",EDGE,{"derivedFrom":sQuery(id+"F5.wireOp",EDGE,"E21.22.0.0")}),-1.0]])]});
            var Q59;
            Q59=makeQuery(id+"F5.imprint","IMPRINT",FACE,{"disambiguationData":[TD([[makeQuery(id+"F5.imprint","IMPRINT",EDGE,{"derivedFrom":sQuery(id+"F5.wireOp",EDGE,"E21.21.0.0")}),-1.0]])]});
            var Q60;
            Q60=makeQuery(id+"F5.imprint","IMPRINT",FACE,{"disambiguationData":[TD([[makeQuery(id+"F5.imprint","IMPRINT",EDGE,{"derivedFrom":sQuery(id+"F5.wireOp",EDGE,"E21.20.0.0")}),-1.0]])]});
            var Q61;
            Q61=makeQuery(id+"F5.imprint","IMPRINT",FACE,{"disambiguationData":[TD([[makeQuery(id+"F5.imprint","IMPRINT",EDGE,{"derivedFrom":sQuery(id+"F5.wireOp",EDGE,"E21.19.0.0")}),-1.0]])]});
            var Q62;
            Q62=makeQuery(id+"F5.imprint","IMPRINT",FACE,{"disambiguationData":[TD([[makeQuery(id+"F5.imprint","IMPRINT",EDGE,{"derivedFrom":sQuery(id+"F5.wireOp",EDGE,"E21.18.0.0")}),-1.0]])]});
            var Q63;
            Q63=makeQuery(id+"F5.imprint","IMPRINT",FACE,{"disambiguationData":[TD([[makeQuery(id+"F5.imprint","IMPRINT",EDGE,{"derivedFrom":sQuery(id+"F5.wireOp",EDGE,"E21.17.0.0")}),-1.0]])]});
            var Q64;
            Q64=makeQuery(id+"F5.imprint","IMPRINT",FACE,{"disambiguationData":[TD([[makeQuery(id+"F5.imprint","IMPRINT",EDGE,{"derivedFrom":sQuery(id+"F5.wireOp",EDGE,"E21.16.0.0")}),-1.0]])]});
            var Q65;
            Q65=makeQuery(id+"F5.imprint","IMPRINT",FACE,{"disambiguationData":[TD([[makeQuery(id+"F5.imprint","IMPRINT",EDGE,{"derivedFrom":sQuery(id+"F5.wireOp",EDGE,"E21.15.0.0")}),-1.0]])]});
            var Q66;
            Q66=makeQuery(id+"F5.imprint","IMPRINT",FACE,{"disambiguationData":[TD([[makeQuery(id+"F5.imprint","IMPRINT",EDGE,{"derivedFrom":sQuery(id+"F5.wireOp",EDGE,"E21.14.0.0")}),-1.0]])]});
            var Q67;
            Q67=makeQuery(id+"F5.imprint","IMPRINT",FACE,{"disambiguationData":[TD([[makeQuery(id+"F5.imprint","IMPRINT",EDGE,{"derivedFrom":sQuery(id+"F5.wireOp",EDGE,"E21.13.0.0")}),-1.0]])]});
            var Q68;
            Q68=makeQuery(id+"F5.imprint","IMPRINT",FACE,{"disambiguationData":[TD([[makeQuery(id+"F5.imprint","IMPRINT",EDGE,{"derivedFrom":sQuery(id+"F5.wireOp",EDGE,"E21.12.0.0")}),-1.0]])]});
            var Q69;
            Q69=makeQuery(id+"F5.imprint","IMPRINT",FACE,{"disambiguationData":[TD([[makeQuery(id+"F5.imprint","IMPRINT",EDGE,{"derivedFrom":sQuery(id+"F5.wireOp",EDGE,"E21.11.0.0")}),-1.0]])]});
            var Q70;
            Q70=makeQuery(id+"F5.imprint","IMPRINT",FACE,{"disambiguationData":[TD([[makeQuery(id+"F5.imprint","IMPRINT",EDGE,{"derivedFrom":sQuery(id+"F5.wireOp",EDGE,"E21.10.0.0")}),-1.0]])]});
            var Q71;
            Q71=makeQuery(id+"F5.imprint","IMPRINT",FACE,{"disambiguationData":[TD([[makeQuery(id+"F5.imprint","IMPRINT",EDGE,{"derivedFrom":sQuery(id+"F5.wireOp",EDGE,"E21.9.0.0")}),-1.0]])]});
            var Q72;
            Q72=makeQuery(id+"F5.imprint","IMPRINT",FACE,{"disambiguationData":[TD([[makeQuery(id+"F5.imprint","IMPRINT",EDGE,{"derivedFrom":sQuery(id+"F5.wireOp",EDGE,"E21.8.0.0")}),-1.0]])]});
            var Q73;
            Q73=makeQuery(id+"F5.imprint","IMPRINT",FACE,{"disambiguationData":[TD([[makeQuery(id+"F5.imprint","IMPRINT",EDGE,{"derivedFrom":sQuery(id+"F5.wireOp",EDGE,"E21.7.0.0")}),-1.0]])]});
            var Q74;
            Q74=makeQuery(id+"F5.imprint","IMPRINT",FACE,{"disambiguationData":[TD([[makeQuery(id+"F5.imprint","IMPRINT",EDGE,{"derivedFrom":sQuery(id+"F5.wireOp",EDGE,"E21.6.0.0")}),-1.0]])]});
            var Q75;
            Q75=makeQuery(id+"F5.imprint","IMPRINT",FACE,{"disambiguationData":[TD([[makeQuery(id+"F5.imprint","IMPRINT",EDGE,{"derivedFrom":sQuery(id+"F5.wireOp",EDGE,"E21.5.0.0")}),-1.0]])]});
            extrude(context, id + "F6", {"entities" : qUnion([Q0, Q1, Q2, Q3, Q4, Q5, Q6, Q7, Q8, Q9, Q10, Q11, Q12, Q13, Q14, Q15, Q16, Q17, Q18, Q19, Q20, Q21, Q22, Q23, Q24, Q25, Q26, Q27, Q28, Q29, Q30, Q31, Q32, Q33, Q34, Q35, Q36, Q37, Q38, Q39, Q40, Q41, Q42, Q43, Q44, Q45, Q46, Q47, Q48, Q49, Q50, Q51, Q52, Q53, Q54, Q55, Q56, Q57, Q58, Q59, Q60, Q61, Q62, Q63, Q64, Q65, Q66, Q67, Q68, Q69, Q70, Q71, Q72, Q73, Q74, Q75]), "depth" : 3048 * mm});
        }
        {
            var Q0;
            {var subQ0=sQuery(id+"F5.wireOp",EDGE,"E18.bottom");Q0=makeQuery(id+"F5.imprint","IMPRINT",FACE,{"disambiguationData":[TD([[makeQuery(id+"F5.imprint","IMPRINT",EDGE,{"derivedFrom":subQ0}),-1.0]])]});}
            var Q1;
            {var subQ0=sQuery(id+"F5.wireOp",EDGE,"E27.bottom");Q1=makeQuery(id+"F5.imprint","IMPRINT",FACE,{"disambiguationData":[TD([[makeQuery(id+"F5.imprint","IMPRINT",EDGE,{"derivedFrom":subQ0}),1.0]])]});}
            var Q2;
            {var subQ3=sQuery(id+"F5.wireOp",EDGE,"E33.bottom");Q2=makeQuery(id+"F5.imprint","IMPRINT",FACE,{"disambiguationData":[TD([[makeQuery(id+"F5.imprint","IMPRINT",EDGE,{"derivedFrom":subQ3}),1.0]])]});}
            var Q3;
            {var subQ0=sQuery(id+"F5.wireOp",EDGE,"E36.bottom");Q3=makeQuery(id+"F5.imprint","IMPRINT",FACE,{"disambiguationData":[TD([[makeQuery(id+"F5.imprint","IMPRINT",EDGE,{"derivedFrom":subQ0}),-1.0]])]});}
            extrude(context, id + "F7", {"entities" : qUnion([Q0, Q1, Q2, Q3]), "depth" : 3048 * mm});
        }
        {
            var Q0;
            {var subQ3=sQuery(id+"F5.wireOp",EDGE,"E28.bottom");Q0=makeQuery(id+"F5.imprint","IMPRINT",FACE,{"disambiguationData":[TD([[makeQuery(id+"F5.imprint","IMPRINT",EDGE,{"derivedFrom":subQ3}),-1.0]])]});}
            var Q1;
            {var subQ3=sQuery(id+"F5.wireOp",EDGE,"E20.bottom");Q1=makeQuery(id+"F5.imprint","IMPRINT",FACE,{"disambiguationData":[TD([[makeQuery(id+"F5.imprint","IMPRINT",EDGE,{"derivedFrom":subQ3}),1.0]])]});}
            var Q2;
            Q2=makeQuery(id+"F5.imprint","IMPRINT",FACE,{"disambiguationData":[TD([[makeQuery(id+"F5.imprint","IMPRINT",EDGE,{"derivedFrom":sQuery(id+"F5.wireOp",EDGE,"E31.bottom")}),-1.0]])]});
            var Q3;
            Q3=makeQuery(id+"F5.imprint","IMPRINT",FACE,{"disambiguationData":[TD([[makeQuery(id+"F5.imprint","IMPRINT",EDGE,{"derivedFrom":sQuery(id+"F5.wireOp",EDGE,"E37.top")}),-1.0]])]});
            extrude(context, id + "F8", {"entities" : qUnion([Q0, Q1, Q2, Q3]), "depth" : 3048 * mm});
        }
        {
            var Q0;
            Q0=makeQuery(id+"F6.opExtrude","CAP_FACE",FACE,{"disambiguationData":[OSD([sQuery(id+"F5.wireOp",EDGE,"E17.bottom"),sQuery(id+"F5.wireOp",EDGE,"E17.top"),sQuery(id+"F5.wireOp",EDGE,"E17.left"),sQuery(id+"F5.wireOp",EDGE,"E18.bottom"),sQuery(id+"F5.wireOp",EDGE,"E20.left")])],"isStart":false});
            var sketch = newSketch(context, id + "F9", { "sketchPlane" : qUnion([Q0])});
            skLineSegment(sketch, "E38.bottom", {"start": v(0, 0) * mm, "end": v(3048, 0) * mm});
            skLineSegment(sketch, "E38.top", {"start": v(0, 139.7) * mm, "end": v(3048, 139.7) * mm});
            skLineSegment(sketch, "E38.left", {"start": v(0, 0) * mm, "end": v(0, 139.7) * mm});
            skLineSegment(sketch, "E38.right", {"start": v(3048, 0) * mm, "end": v(3048, 139.7) * mm});
            skLineSegment(sketch, "E39.bottom", {"start": v(3048, 0) * mm, "end": v(6096, 0) * mm});
            skLineSegment(sketch, "E39.top", {"start": v(3048, 139.7) * mm, "end": v(6096, 139.7) * mm});
            skLineSegment(sketch, "E39.right", {"start": v(6096, 0) * mm, "end": v(6096, 139.7) * mm});
            skLineSegment(sketch, "E40.bottom", {"start": v(6096, 0) * mm, "end": v(9144, 0) * mm});
            skLineSegment(sketch, "E40.top", {"start": v(6096, 139.7) * mm, "end": v(9144, 139.7) * mm});
            skLineSegment(sketch, "E40.right", {"start": v(9144, 0) * mm, "end": v(9144, 139.7) * mm});
            skLineSegment(sketch, "E41.bottom", {"start": v(9144, 0) * mm, "end": v(12192, 0) * mm});
            skLineSegment(sketch, "E41.top", {"start": v(9144, 139.7) * mm, "end": v(12192, 139.7) * mm});
            skLineSegment(sketch, "E41.right", {"start": v(12192, 0) * mm, "end": v(12192, 139.7) * mm});
            skPoint(sketch, "E42.0", {"position": v(14630.4, 0) * mm});
            skLineSegment(sketch, "E43.bottom", {"start": v(12192, 0) * mm, "end": v(14630.4, 0) * mm});
            skLineSegment(sketch, "E43.top", {"start": v(12192, 139.7) * mm, "end": v(14630.4, 139.7) * mm});
            skLineSegment(sketch, "E43.right", {"start": v(14630.4, 0) * mm, "end": v(14630.4, 139.7) * mm});
            skPoint(sketch, "E44.0", {"position": v(14490.7, 177.8) * mm});
            skLineSegment(sketch, "E45.bottom", {"start": v(14630.4, 139.7) * mm, "end": v(14490.7, 139.7) * mm});
            skLineSegment(sketch, "E45.top", {"start": v(14630.4, 3187.7) * mm, "end": v(14490.7, 3187.7) * mm});
            skLineSegment(sketch, "E45.left", {"start": v(14630.4, 139.7) * mm, "end": v(14630.4, 3187.7) * mm});
            skLineSegment(sketch, "E45.right", {"start": v(14490.7, 139.7) * mm, "end": v(14490.7, 3187.7) * mm});
            skLineSegment(sketch, "E46.bottom", {"start": v(14490.7, 3187.7) * mm, "end": v(14630.4, 3187.7) * mm});
            skLineSegment(sketch, "E46.top", {"start": v(14490.7, 6235.7) * mm, "end": v(14630.4, 6235.7) * mm});
            skLineSegment(sketch, "E46.left", {"start": v(14490.7, 3187.7) * mm, "end": v(14490.7, 6235.7) * mm});
            skLineSegment(sketch, "E46.right", {"start": v(14630.4, 3187.7) * mm, "end": v(14630.4, 6235.7) * mm});
            skPoint(sketch, "E47.0", {"position": v(14630.4, 8534.4) * mm});
            skLineSegment(sketch, "E48.top", {"start": v(14490.7, 8534.4) * mm, "end": v(14630.4, 8534.4) * mm});
            skLineSegment(sketch, "E48.left", {"start": v(14490.7, 6235.7) * mm, "end": v(14490.7, 8534.4) * mm});
            skLineSegment(sketch, "E48.right", {"start": v(14630.4, 6235.7) * mm, "end": v(14630.4, 8534.4) * mm});
            skPoint(sketch, "E49.0", {"position": v(14452.6, 8394.7) * mm});
            skLineSegment(sketch, "E50.bottom", {"start": v(14490.7, 8534.4) * mm, "end": v(11442.7, 8534.4) * mm});
            skLineSegment(sketch, "E50.top", {"start": v(14490.7, 8394.7) * mm, "end": v(11442.7, 8394.7) * mm});
            skLineSegment(sketch, "E50.left", {"start": v(14490.7, 8534.4) * mm, "end": v(14490.7, 8394.7) * mm});
            skLineSegment(sketch, "E50.right", {"start": v(11442.7, 8534.4) * mm, "end": v(11442.7, 8394.7) * mm});
            skLineSegment(sketch, "E51.bottom", {"start": v(11442.7, 8394.7) * mm, "end": v(8394.7, 8394.7) * mm});
            skLineSegment(sketch, "E51.top", {"start": v(11442.7, 8534.4) * mm, "end": v(8394.7, 8534.4) * mm});
            skLineSegment(sketch, "E51.left", {"start": v(11442.7, 8394.7) * mm, "end": v(11442.7, 8534.4) * mm});
            skLineSegment(sketch, "E51.right", {"start": v(8394.7, 8394.7) * mm, "end": v(8394.7, 8534.4) * mm});
            skLineSegment(sketch, "E52.bottom", {"start": v(8394.7, 8394.7) * mm, "end": v(5346.7, 8394.7) * mm});
            skLineSegment(sketch, "E52.top", {"start": v(8394.7, 8534.4) * mm, "end": v(5346.7, 8534.4) * mm});
            skLineSegment(sketch, "E52.right", {"start": v(5346.7, 8394.7) * mm, "end": v(5346.7, 8534.4) * mm});
            skLineSegment(sketch, "E53.bottom", {"start": v(5346.7, 8394.7) * mm, "end": v(2298.7, 8394.7) * mm});
            skLineSegment(sketch, "E53.top", {"start": v(5346.7, 8534.4) * mm, "end": v(2298.7, 8534.4) * mm});
            skLineSegment(sketch, "E53.right", {"start": v(2298.7, 8394.7) * mm, "end": v(2298.7, 8534.4) * mm});
            skPoint(sketch, "E54.0", {"position": v(0, 8534.4) * mm});
            skLineSegment(sketch, "E55.bottom", {"start": v(2298.7, 8394.7) * mm, "end": v(0, 8394.7) * mm});
            skLineSegment(sketch, "E55.top", {"start": v(2298.7, 8534.4) * mm, "end": v(0, 8534.4) * mm});
            skLineSegment(sketch, "E55.right", {"start": v(0, 8394.7) * mm, "end": v(0, 8534.4) * mm});
            skPoint(sketch, "E56.0", {"position": v(139.7, 8356.6) * mm});
            skLineSegment(sketch, "E57.bottom", {"start": v(0, 8394.7) * mm, "end": v(139.7, 8394.7) * mm});
            skLineSegment(sketch, "E57.top", {"start": v(0, 5346.7) * mm, "end": v(139.7, 5346.7) * mm});
            skLineSegment(sketch, "E57.left", {"start": v(0, 8394.7) * mm, "end": v(0, 5346.7) * mm});
            skLineSegment(sketch, "E57.right", {"start": v(139.7, 8394.7) * mm, "end": v(139.7, 5346.7) * mm});
            skLineSegment(sketch, "E58.top", {"start": v(0, 2298.7) * mm, "end": v(139.7, 2298.7) * mm});
            skLineSegment(sketch, "E58.left", {"start": v(0, 5346.7) * mm, "end": v(0, 2298.7) * mm});
            skLineSegment(sketch, "E58.right", {"start": v(139.7, 5346.7) * mm, "end": v(139.7, 2298.7) * mm});
            skLineSegment(sketch, "E59.bottom", {"start": v(139.7, 2298.7) * mm, "end": v(0, 2298.7) * mm});
            skLineSegment(sketch, "E59.top", {"start": v(139.7, 139.7) * mm, "end": v(0, 139.7) * mm});
            skLineSegment(sketch, "E59.left", {"start": v(139.7, 2298.7) * mm, "end": v(139.7, 139.7) * mm});
            skLineSegment(sketch, "E59.right", {"start": v(0, 2298.7) * mm, "end": v(0, 139.7) * mm});
            skSolve(sketch);
        }
        {
            var Q0;
            Q0=makeQuery(id+"F9.imprint","IMPRINT",FACE,{"disambiguationData":[TD([[makeQuery(id+"F9.imprint","IMPRINT",EDGE,{"derivedFrom":sQuery(id+"F9.wireOp",EDGE,"E38.top")}),-1.0]])]});
            var Q1;
            Q1=makeQuery(id+"F9.imprint","IMPRINT",FACE,{"disambiguationData":[TD([[makeQuery(id+"F9.imprint","IMPRINT",EDGE,{"derivedFrom":sQuery(id+"F9.wireOp",EDGE,"E40.bottom")}),1.0]])]});
            var Q2;
            Q2=makeQuery(id+"F9.imprint","IMPRINT",FACE,{"disambiguationData":[TD([[makeQuery(id+"F9.imprint","IMPRINT",EDGE,{"derivedFrom":sQuery(id+"F9.wireOp",EDGE,"E43.bottom")}),1.0]])]});
            var Q3;
            Q3=makeQuery(id+"F9.imprint","IMPRINT",FACE,{"disambiguationData":[TD([[makeQuery(id+"F9.imprint","IMPRINT",EDGE,{"derivedFrom":sQuery(id+"F9.wireOp",EDGE,"E46.bottom")}),1.0]])]});
            var Q4;
            Q4=makeQuery(id+"F9.imprint","IMPRINT",FACE,{"disambiguationData":[TD([[makeQuery(id+"F9.imprint","IMPRINT",EDGE,{"derivedFrom":sQuery(id+"F9.wireOp",EDGE,"E50.bottom")}),1.0]])]});
            var Q5;
            Q5=makeQuery(id+"F9.imprint","IMPRINT",FACE,{"disambiguationData":[TD([[makeQuery(id+"F9.imprint","IMPRINT",EDGE,{"derivedFrom":sQuery(id+"F9.wireOp",EDGE,"E52.bottom")}),-1.0]])]});
            var Q6;
            Q6=makeQuery(id+"F9.imprint","IMPRINT",FACE,{"disambiguationData":[TD([[makeQuery(id+"F9.imprint","IMPRINT",EDGE,{"derivedFrom":sQuery(id+"F9.wireOp",EDGE,"E55.bottom")}),-1.0]])]});
            var Q7;
            Q7=makeQuery(id+"F9.imprint","IMPRINT",FACE,{"disambiguationData":[TD([[makeQuery(id+"F9.imprint","IMPRINT",EDGE,{"derivedFrom":sQuery(id+"F9.wireOp",EDGE,"E57.top")}),-1.0]])]});
            var Q8;
            {var subQ3=makeQuery(id+"F6.opExtrude","CAP_EDGE",EDGE,{"disambiguationData":[OSD([sQuery(id+"F5.wireOp",EDGE,"E20.left")])],"isStart":false});Q8=makeQuery(id+"F9.imprint","IMPRINT",FACE,{"disambiguationData":[TD([[makeQuery(id+"F9.imprint","IMPRINT",EDGE,{"derivedFrom":subQ3}),-1.0]])]});}
            extrude(context, id + "F10", {"entities" : qUnion([Q0, Q1, Q2, Q3, Q4, Q5, Q6, Q7, Q8]), "depth" : 38.1 * mm});
        }
        {
            var Q0;
            Q0=makeQuery(id+"F9.imprint","IMPRINT",FACE,{"disambiguationData":[TD([[makeQuery(id+"F9.imprint","IMPRINT",EDGE,{"derivedFrom":sQuery(id+"F9.wireOp",EDGE,"E59.bottom")}),1.0]])]});
            var Q1;
            Q1=makeQuery(id+"F9.imprint","IMPRINT",FACE,{"disambiguationData":[TD([[makeQuery(id+"F9.imprint","IMPRINT",EDGE,{"derivedFrom":sQuery(id+"F9.wireOp",EDGE,"E57.bottom")}),-1.0]])]});
            var Q2;
            Q2=makeQuery(id+"F9.imprint","IMPRINT",FACE,{"disambiguationData":[TD([[makeQuery(id+"F9.imprint","IMPRINT",EDGE,{"derivedFrom":sQuery(id+"F9.wireOp",EDGE,"E53.bottom")}),-1.0]])]});
            var Q3;
            Q3=makeQuery(id+"F9.imprint","IMPRINT",FACE,{"disambiguationData":[TD([[makeQuery(id+"F9.imprint","IMPRINT",EDGE,{"derivedFrom":sQuery(id+"F9.wireOp",EDGE,"E39.bottom")}),1.0]])]});
            var Q4;
            Q4=makeQuery(id+"F9.imprint","IMPRINT",FACE,{"disambiguationData":[TD([[makeQuery(id+"F9.imprint","IMPRINT",EDGE,{"derivedFrom":sQuery(id+"F9.wireOp",EDGE,"E41.bottom")}),1.0]])]});
            var Q5;
            Q5=makeQuery(id+"F9.imprint","IMPRINT",FACE,{"disambiguationData":[TD([[makeQuery(id+"F9.imprint","IMPRINT",EDGE,{"derivedFrom":sQuery(id+"F9.wireOp",EDGE,"E45.bottom")}),-1.0]])]});
            var Q6;
            Q6=makeQuery(id+"F9.imprint","IMPRINT",FACE,{"disambiguationData":[TD([[makeQuery(id+"F9.imprint","IMPRINT",EDGE,{"derivedFrom":sQuery(id+"F9.wireOp",EDGE,"E46.top")}),1.0]])]});
            var Q7;
            Q7=makeQuery(id+"F9.imprint","IMPRINT",FACE,{"disambiguationData":[TD([[makeQuery(id+"F9.imprint","IMPRINT",EDGE,{"derivedFrom":sQuery(id+"F9.wireOp",EDGE,"E51.bottom")}),-1.0]])]});
            extrude(context, id + "F11", {"entities" : qUnion([Q0, Q1, Q2, Q3, Q4, Q5, Q6, Q7]), "depth" : 38.1 * mm});
        }
        {
            var Q0;
            Q0=makeQuery(id+"F3.opExtrude","SWEPT_FACE",FACE,{"disambiguationData":[OSD([sQuery(id+"F2.wireOp",EDGE,"E1.left")])]});
            var sketch = newSketch(context, id + "F12", { "sketchPlane" : qUnion([Q0])});
            skLineSegment(sketch, "E60.0", {"start": v(-1866.9, 38.1) * mm, "end": v(-1828.8, 38.1) * mm, "construction": true});
            skPoint(sketch, "E61.oppositeSnap0", {"position": v(-1847.85, 38.1) * mm});
            skLineSegment(sketch, "E61.bottom", {"start": v(0, 0) * mm, "end": v(-1847.85, 0) * mm});
            skLineSegment(sketch, "E61.top", {"start": v(0, 1219.2) * mm, "end": v(-1847.85, 1219.2) * mm});
            skLineSegment(sketch, "E61.left", {"start": v(0, 0) * mm, "end": v(0, 1219.2) * mm});
            skLineSegment(sketch, "E61.right", {"start": v(-1847.85, 0) * mm, "end": v(-1847.85, 1219.2) * mm});
            skLineSegment(sketch, "E62.bottom", {"start": v(-1847.85, 0) * mm, "end": v(-4286.25, 0) * mm});
            skLineSegment(sketch, "E62.top", {"start": v(-1847.85, 1219.2) * mm, "end": v(-4286.25, 1219.2) * mm});
            skLineSegment(sketch, "E62.right", {"start": v(-4286.25, 0) * mm, "end": v(-4286.25, 1219.2) * mm});
            skLineSegment(sketch, "E63.bottom", {"start": v(-4286.25, 0) * mm, "end": v(-6724.65, 0) * mm});
            skLineSegment(sketch, "E63.top", {"start": v(-4286.25, 1219.2) * mm, "end": v(-6724.65, 1219.2) * mm});
            skLineSegment(sketch, "E63.right", {"start": v(-6724.65, 0) * mm, "end": v(-6724.65, 1219.2) * mm});
            skLineSegment(sketch, "E64.0", {"start": v(-8534.4, 38.1) * mm, "end": v(-8496.3, 38.1) * mm, "construction": true});
            skLineSegment(sketch, "E65.bottom", {"start": v(-6724.65, 1219.2) * mm, "end": v(-8534.4, 1219.2) * mm});
            skLineSegment(sketch, "E65.top", {"start": v(-6724.65, 0) * mm, "end": v(-8534.4, 0) * mm});
            skLineSegment(sketch, "E65.left", {"start": v(-6724.65, 1219.2) * mm, "end": v(-6724.65, 0) * mm});
            skLineSegment(sketch, "E65.right", {"start": v(-8534.4, 1219.2) * mm, "end": v(-8534.4, 0) * mm});
            skLineSegment(sketch, "E66.0", {"start": v(-1257.3, 38.1) * mm, "end": v(-1219.2, 38.1) * mm, "construction": true});
            skPoint(sketch, "E67.oppositeSnap0", {"position": v(-1238.25, 38.1) * mm});
            skLineSegment(sketch, "E67.bottom", {"start": v(0, 1219.2) * mm, "end": v(-1238.25, 1219.2) * mm});
            skLineSegment(sketch, "E67.top", {"start": v(0, 2438.4) * mm, "end": v(-1238.25, 2438.4) * mm});
            skLineSegment(sketch, "E67.left", {"start": v(0, 1219.2) * mm, "end": v(0, 2438.4) * mm});
            skLineSegment(sketch, "E67.right", {"start": v(-1238.25, 1219.2) * mm, "end": v(-1238.25, 2438.4) * mm});
            skLineSegment(sketch, "E68.bottom", {"start": v(-1238.25, 2438.4) * mm, "end": v(-3676.65, 2438.4) * mm});
            skLineSegment(sketch, "E68.top", {"start": v(-1238.25, 1219.2) * mm, "end": v(-3676.65, 1219.2) * mm});
            skLineSegment(sketch, "E68.left", {"start": v(-1238.25, 2438.4) * mm, "end": v(-1238.25, 1219.2) * mm});
            skLineSegment(sketch, "E68.right", {"start": v(-3676.65, 2438.4) * mm, "end": v(-3676.65, 1219.2) * mm});
            skLineSegment(sketch, "E69.bottom", {"start": v(-3676.65, 2438.4) * mm, "end": v(-6115.05, 2438.4) * mm});
            skLineSegment(sketch, "E69.top", {"start": v(-3676.65, 1219.2) * mm, "end": v(-6115.05, 1219.2) * mm});
            skLineSegment(sketch, "E69.right", {"start": v(-6115.05, 2438.4) * mm, "end": v(-6115.05, 1219.2) * mm});
            skLineSegment(sketch, "E70.bottom", {"start": v(-6115.05, 2438.4) * mm, "end": v(-8534.4, 2438.4) * mm});
            skLineSegment(sketch, "E70.top", {"start": v(-6115.05, 1219.2) * mm, "end": v(-8534.4, 1219.2) * mm});
            skLineSegment(sketch, "E70.right", {"start": v(-8534.4, 2438.4) * mm, "end": v(-8534.4, 1219.2) * mm});
            skLineSegment(sketch, "E71.0", {"start": v(0, 3124.2) * mm, "end": v(-139.7, 3124.2) * mm, "construction": true});
            skPoint(sketch, "E72.oppositeSnap0", {"position": v(-69.85, 3124.2) * mm});
            skLineSegment(sketch, "E72.bottom", {"start": v(0, 2438.4) * mm, "end": v(-1847.85, 2438.4) * mm});
            skLineSegment(sketch, "E72.top", {"start": v(0, 3124.2) * mm, "end": v(-1847.85, 3124.2) * mm});
            skLineSegment(sketch, "E72.left", {"start": v(0, 2438.4) * mm, "end": v(0, 3124.2) * mm});
            skLineSegment(sketch, "E72.right", {"start": v(-1847.85, 2438.4) * mm, "end": v(-1847.85, 3124.2) * mm});
            skLineSegment(sketch, "E73.bottom", {"start": v(-1847.85, 3124.2) * mm, "end": v(-4286.25, 3124.2) * mm});
            skLineSegment(sketch, "E73.top", {"start": v(-1847.85, 2438.4) * mm, "end": v(-4286.25, 2438.4) * mm});
            skLineSegment(sketch, "E73.left", {"start": v(-1847.85, 3124.2) * mm, "end": v(-1847.85, 2438.4) * mm});
            skLineSegment(sketch, "E73.right", {"start": v(-4286.25, 3124.2) * mm, "end": v(-4286.25, 2438.4) * mm});
            skLineSegment(sketch, "E74.bottom", {"start": v(-4286.25, 3124.2) * mm, "end": v(-6724.65, 3124.2) * mm});
            skLineSegment(sketch, "E74.top", {"start": v(-4286.25, 2438.4) * mm, "end": v(-6724.65, 2438.4) * mm});
            skLineSegment(sketch, "E74.right", {"start": v(-6724.65, 3124.2) * mm, "end": v(-6724.65, 2438.4) * mm});
            skLineSegment(sketch, "E75.bottom", {"start": v(-6724.65, 3124.2) * mm, "end": v(-8534.4, 3124.2) * mm});
            skLineSegment(sketch, "E75.top", {"start": v(-6724.65, 2438.4) * mm, "end": v(-8534.4, 2438.4) * mm});
            skLineSegment(sketch, "E75.right", {"start": v(-8534.4, 3124.2) * mm, "end": v(-8534.4, 2438.4) * mm});
            skSolve(sketch);
        }
        {
            var Q0;
            {var subQ0=sQuery(id+"F12.wireOp",EDGE,"E67.bottom");Q0=makeQuery(id+"F12.imprint","IMPRINT",FACE,{"disambiguationData":[TD([[makeQuery(id+"F12.imprint","IMPRINT",EDGE,{"derivedFrom":subQ0}),1.0]])]});}
            var Q1;
            Q1=makeQuery(id+"F12.imprint","IMPRINT",FACE,{"disambiguationData":[TD([[makeQuery(id+"F12.imprint","IMPRINT",EDGE,{"derivedFrom":sQuery(id+"F12.wireOp",EDGE,"E72.top")}),1.0]])]});
            var Q2;
            Q2=makeQuery(id+"F12.imprint","IMPRINT",FACE,{"disambiguationData":[TD([[makeQuery(id+"F12.imprint","IMPRINT",EDGE,{"derivedFrom":sQuery(id+"F12.wireOp",EDGE,"E63.bottom")}),-1.0]])]});
            var Q3;
            Q3=makeQuery(id+"F12.imprint","IMPRINT",FACE,{"disambiguationData":[TD([[makeQuery(id+"F12.imprint","IMPRINT",EDGE,{"derivedFrom":sQuery(id+"F12.wireOp",EDGE,"E74.bottom")}),1.0]])]});
            var Q4;
            {var subQ0=sQuery(id+"F12.wireOp",EDGE,"E61.bottom");Q4=makeQuery(id+"F12.imprint","IMPRINT",FACE,{"disambiguationData":[TD([[makeQuery(id+"F12.imprint","IMPRINT",EDGE,{"derivedFrom":subQ0}),1.0]])]});}
            extrude(context, id + "F13", {"entities" : qUnion([Q0, Q1, Q2, Q3, Q4]), "depth" : 15.88 * mm});
        }
        {
            var Q0;
            Q0=makeQuery(id+"F12.imprint","IMPRINT",FACE,{"disambiguationData":[TD([[makeQuery(id+"F12.imprint","IMPRINT",EDGE,{"derivedFrom":sQuery(id+"F12.wireOp",EDGE,"E67.bottom")}),-1.0]])]});
            var Q1;
            Q1=makeQuery(id+"F12.imprint","IMPRINT",FACE,{"disambiguationData":[TD([[makeQuery(id+"F12.imprint","IMPRINT",EDGE,{"derivedFrom":sQuery(id+"F12.wireOp",EDGE,"E73.bottom")}),1.0]])]});
            var Q2;
            {var subQ5=sQuery(id+"F12.wireOp",EDGE,"E62.right");Q2=makeQuery(id+"F12.imprint","IMPRINT",FACE,{"disambiguationData":[TD([[makeQuery(id+"F12.imprint","IMPRINT",EDGE,{"derivedFrom":subQ5}),-1.0]])]});}
            var Q3;
            Q3=makeQuery(id+"F12.imprint","IMPRINT",FACE,{"disambiguationData":[TD([[makeQuery(id+"F12.imprint","IMPRINT",EDGE,{"derivedFrom":sQuery(id+"F12.wireOp",EDGE,"E65.top")}),-1.0]])]});
            var Q4;
            Q4=makeQuery(id+"F12.imprint","IMPRINT",FACE,{"disambiguationData":[TD([[makeQuery(id+"F12.imprint","IMPRINT",EDGE,{"derivedFrom":sQuery(id+"F12.wireOp",EDGE,"E75.bottom")}),1.0]])]});
            var Q5;
            {var subQ1=sQuery(id+"F2.wireOp",EDGE,"E1.left");var subQ2=makeQuery(id+"F3.opExtrude","SWEPT_EDGE",EDGE,{"disambiguationData":[OSD([subQ1,sQuery(id+"F2.wireOp",EDGE,"E7.bottom"),sQuery(id+"F2.wireOp",EDGE,"E7.right")])]});Q5=makeQuery(id+"F12.imprint","IMPRINT",FACE,{"disambiguationData":[TD([[makeQuery(id+"F12.imprint","IMPRINT",EDGE,{"derivedFrom":subQ2}),1.0]])]});}
            extrude(context, id + "F14", {"entities" : qUnion([Q0, Q1, Q2, Q3, Q4, Q5]), "depth" : 15.88 * mm});
        }
        {
            var Q0;
            {var subQ4=sQuery(id+"F12.wireOp",EDGE,"E68.left");Q0=makeQuery(id+"F12.imprint","IMPRINT",FACE,{"disambiguationData":[TD([[makeQuery(id+"F12.imprint","IMPRINT",EDGE,{"derivedFrom":subQ4}),-1.0]])]});}
            var Q1;
            {var subQ1=sQuery(id+"F12.wireOp",EDGE,"E69.right");Q1=makeQuery(id+"F12.imprint","IMPRINT",FACE,{"disambiguationData":[TD([[makeQuery(id+"F12.imprint","IMPRINT",EDGE,{"derivedFrom":subQ1}),-1.0]])]});}
            extrude(context, id + "F15", {"entities" : qUnion([Q0, Q1]), "depth" : 15.88 * mm});
        }
        {
            var Q0;
            {var subQ0=sQuery(id+"F12.wireOp",EDGE,"E68.right");Q0=makeQuery(id+"F12.imprint","IMPRINT",FACE,{"disambiguationData":[TD([[makeQuery(id+"F12.imprint","IMPRINT",EDGE,{"derivedFrom":subQ0}),-1.0]])]});}
            extrude(context, id + "F16", {"entities" : qUnion([Q0]), "depth" : 15.88 * mm});
        }
        {
            var Q0;
            Q0=makeQuery(id+"F3.opExtrude","SWEPT_FACE",FACE,{"disambiguationData":[OSD([sQuery(id+"F2.wireOp",EDGE,"E8.top")])]});
            var sketch = newSketch(context, id + "F17", { "sketchPlane" : qUnion([Q0])});
            skPoint(sketch, "E76.0", {"position": v(15.88, 0) * mm});
            skLineSegment(sketch, "E77.0", {"start": v(-1968.5, 38.1) * mm, "end": v(-2006.6, 38.1) * mm, "construction": true});
            skPoint(sketch, "E78.oppositeSnap0", {"position": v(-1987.55, 38.1) * mm});
            skLineSegment(sketch, "E78.bottom", {"start": v(15.88, 0) * mm, "end": v(-1987.55, 0) * mm});
            skLineSegment(sketch, "E78.top", {"start": v(15.88, 1219.2) * mm, "end": v(-1987.55, 1219.2) * mm});
            skLineSegment(sketch, "E78.left", {"start": v(15.88, 0) * mm, "end": v(15.88, 1219.2) * mm});
            skLineSegment(sketch, "E78.right", {"start": v(-1987.55, 0) * mm, "end": v(-1987.55, 1219.2) * mm});
            skLineSegment(sketch, "E79.0", {"start": v(-749.3, 38.1) * mm, "end": v(-787.4, 38.1) * mm, "construction": true});
            skPoint(sketch, "E80.oppositeSnap0", {"position": v(-768.35, 38.1) * mm});
            skLineSegment(sketch, "E80.bottom", {"start": v(15.88, 1219.2) * mm, "end": v(-768.35, 1219.2) * mm});
            skLineSegment(sketch, "E80.top", {"start": v(15.88, 2438.4) * mm, "end": v(-768.35, 2438.4) * mm});
            skLineSegment(sketch, "E80.left", {"start": v(15.88, 1219.2) * mm, "end": v(15.88, 2438.4) * mm});
            skLineSegment(sketch, "E80.right", {"start": v(-768.35, 1219.2) * mm, "end": v(-768.35, 2438.4) * mm});
            skLineSegment(sketch, "E81.bottom", {"start": v(-1987.55, 0) * mm, "end": v(-4425.95, 0) * mm});
            skLineSegment(sketch, "E81.top", {"start": v(-1987.55, 1219.2) * mm, "end": v(-4425.95, 1219.2) * mm});
            skLineSegment(sketch, "E81.right", {"start": v(-4425.95, 0) * mm, "end": v(-4425.95, 1219.2) * mm});
            skLineSegment(sketch, "E82.bottom", {"start": v(-768.35, 1219.2) * mm, "end": v(-3206.75, 1219.2) * mm});
            skLineSegment(sketch, "E82.top", {"start": v(-768.35, 2438.4) * mm, "end": v(-3206.75, 2438.4) * mm});
            skLineSegment(sketch, "E82.right", {"start": v(-3206.75, 1219.2) * mm, "end": v(-3206.75, 2438.4) * mm});
            skPoint(sketch, "E83.0", {"position": v(15.88, 3124.2) * mm});
            skLineSegment(sketch, "E84.bottom", {"start": v(15.88, 2438.4) * mm, "end": v(-1987.55, 2438.4) * mm});
            skLineSegment(sketch, "E84.top", {"start": v(15.88, 3124.2) * mm, "end": v(-1987.55, 3124.2) * mm});
            skLineSegment(sketch, "E84.left", {"start": v(15.88, 2438.4) * mm, "end": v(15.88, 3124.2) * mm});
            skLineSegment(sketch, "E84.right", {"start": v(-1987.55, 2438.4) * mm, "end": v(-1987.55, 3124.2) * mm});
            skLineSegment(sketch, "E85.bottom", {"start": v(-4425.95, 0) * mm, "end": v(-6864.35, 0) * mm});
            skLineSegment(sketch, "E85.top", {"start": v(-4425.95, 1219.2) * mm, "end": v(-6864.35, 1219.2) * mm});
            skLineSegment(sketch, "E85.right", {"start": v(-6864.35, 0) * mm, "end": v(-6864.35, 1219.2) * mm});
            skLineSegment(sketch, "E86.bottom", {"start": v(-6864.35, 0) * mm, "end": v(-9302.75, 0) * mm});
            skLineSegment(sketch, "E86.top", {"start": v(-6864.35, 1219.2) * mm, "end": v(-9302.75, 1219.2) * mm});
            skLineSegment(sketch, "E86.right", {"start": v(-9302.75, 0) * mm, "end": v(-9302.75, 1219.2) * mm});
            skLineSegment(sketch, "E87.bottom", {"start": v(-9302.75, 0) * mm, "end": v(-11741.15, 0) * mm});
            skLineSegment(sketch, "E87.top", {"start": v(-9302.75, 1219.2) * mm, "end": v(-11741.15, 1219.2) * mm});
            skLineSegment(sketch, "E87.right", {"start": v(-11741.15, 0) * mm, "end": v(-11741.15, 1219.2) * mm});
            skLineSegment(sketch, "E88.bottom", {"start": v(-11741.15, 0) * mm, "end": v(-14179.55, 0) * mm});
            skLineSegment(sketch, "E88.top", {"start": v(-11741.15, 1219.2) * mm, "end": v(-14179.55, 1219.2) * mm});
            skLineSegment(sketch, "E88.right", {"start": v(-14179.55, 0) * mm, "end": v(-14179.55, 1219.2) * mm});
            skPoint(sketch, "E89.0", {"position": v(-14630.4, 0) * mm});
            skLineSegment(sketch, "E90.bottom", {"start": v(-14179.55, 1219.2) * mm, "end": v(-14630.4, 1219.2) * mm});
            skLineSegment(sketch, "E90.top", {"start": v(-14179.55, 0) * mm, "end": v(-14630.4, 0) * mm});
            skLineSegment(sketch, "E90.left", {"start": v(-14179.55, 1219.2) * mm, "end": v(-14179.55, 0) * mm});
            skLineSegment(sketch, "E90.right", {"start": v(-14630.4, 1219.2) * mm, "end": v(-14630.4, 0) * mm});
            skLineSegment(sketch, "E91.bottom", {"start": v(-3206.75, 2438.4) * mm, "end": v(-5645.15, 2438.4) * mm});
            skLineSegment(sketch, "E91.top", {"start": v(-3206.75, 1219.2) * mm, "end": v(-5645.15, 1219.2) * mm});
            skLineSegment(sketch, "E91.left", {"start": v(-3206.75, 2438.4) * mm, "end": v(-3206.75, 1219.2) * mm});
            skLineSegment(sketch, "E91.right", {"start": v(-5645.15, 2438.4) * mm, "end": v(-5645.15, 1219.2) * mm});
            skLineSegment(sketch, "E92.bottom", {"start": v(-5645.15, 2438.4) * mm, "end": v(-8083.55, 2438.4) * mm});
            skLineSegment(sketch, "E92.top", {"start": v(-5645.15, 1219.2) * mm, "end": v(-8083.55, 1219.2) * mm});
            skLineSegment(sketch, "E92.right", {"start": v(-8083.55, 2438.4) * mm, "end": v(-8083.55, 1219.2) * mm});
            skLineSegment(sketch, "E93.bottom", {"start": v(-8083.55, 2438.4) * mm, "end": v(-10521.95, 2438.4) * mm});
            skLineSegment(sketch, "E93.top", {"start": v(-8083.55, 1219.2) * mm, "end": v(-10521.95, 1219.2) * mm});
            skLineSegment(sketch, "E93.right", {"start": v(-10521.95, 2438.4) * mm, "end": v(-10521.95, 1219.2) * mm});
            skLineSegment(sketch, "E94.bottom", {"start": v(-1987.55, 2438.4) * mm, "end": v(-4425.95, 2438.4) * mm});
            skLineSegment(sketch, "E94.top", {"start": v(-1987.55, 3124.2) * mm, "end": v(-4425.95, 3124.2) * mm});
            skLineSegment(sketch, "E94.right", {"start": v(-4425.95, 2438.4) * mm, "end": v(-4425.95, 3124.2) * mm});
            skLineSegment(sketch, "E95.bottom", {"start": v(-4425.95, 2438.4) * mm, "end": v(-6864.35, 2438.4) * mm});
            skLineSegment(sketch, "E95.top", {"start": v(-4425.95, 3124.2) * mm, "end": v(-6864.35, 3124.2) * mm});
            skLineSegment(sketch, "E95.right", {"start": v(-6864.35, 2438.4) * mm, "end": v(-6864.35, 3124.2) * mm});
            skLineSegment(sketch, "E96.bottom", {"start": v(-6864.35, 2438.4) * mm, "end": v(-9302.75, 2438.4) * mm});
            skLineSegment(sketch, "E96.top", {"start": v(-6864.35, 3124.2) * mm, "end": v(-9302.75, 3124.2) * mm});
            skLineSegment(sketch, "E96.right", {"start": v(-9302.75, 2438.4) * mm, "end": v(-9302.75, 3124.2) * mm});
            skLineSegment(sketch, "E97.bottom", {"start": v(-10521.95, 2438.4) * mm, "end": v(-12960.35, 2438.4) * mm});
            skLineSegment(sketch, "E97.top", {"start": v(-10521.95, 1219.2) * mm, "end": v(-12960.35, 1219.2) * mm});
            skLineSegment(sketch, "E97.right", {"start": v(-12960.35, 2438.4) * mm, "end": v(-12960.35, 1219.2) * mm});
            skLineSegment(sketch, "E98.bottom", {"start": v(-12960.35, 2438.4) * mm, "end": v(-14630.4, 2438.4) * mm});
            skLineSegment(sketch, "E98.top", {"start": v(-12960.35, 1219.2) * mm, "end": v(-14630.4, 1219.2) * mm});
            skLineSegment(sketch, "E98.right", {"start": v(-14630.4, 2438.4) * mm, "end": v(-14630.4, 1219.2) * mm});
            skLineSegment(sketch, "E99.bottom", {"start": v(-9302.75, 3124.2) * mm, "end": v(-11741.15, 3124.2) * mm});
            skLineSegment(sketch, "E99.top", {"start": v(-9302.75, 2438.4) * mm, "end": v(-11741.15, 2438.4) * mm});
            skLineSegment(sketch, "E99.left", {"start": v(-9302.75, 3124.2) * mm, "end": v(-9302.75, 2438.4) * mm});
            skLineSegment(sketch, "E99.right", {"start": v(-11741.15, 3124.2) * mm, "end": v(-11741.15, 2438.4) * mm});
            skLineSegment(sketch, "E100.bottom", {"start": v(-11741.15, 3124.2) * mm, "end": v(-14179.55, 3124.2) * mm});
            skLineSegment(sketch, "E100.top", {"start": v(-11741.15, 2438.4) * mm, "end": v(-14179.55, 2438.4) * mm});
            skLineSegment(sketch, "E100.right", {"start": v(-14179.55, 3124.2) * mm, "end": v(-14179.55, 2438.4) * mm});
            skLineSegment(sketch, "E101.bottom", {"start": v(-14179.55, 3124.2) * mm, "end": v(-14630.4, 3124.2) * mm});
            skLineSegment(sketch, "E101.top", {"start": v(-14179.55, 2438.4) * mm, "end": v(-14630.4, 2438.4) * mm});
            skLineSegment(sketch, "E101.right", {"start": v(-14630.4, 3124.2) * mm, "end": v(-14630.4, 2438.4) * mm});
            skSolve(sketch);
        }
        {
            var Q0;
            {var subQ1=sQuery(id+"F2.wireOp",EDGE,"E8.top");Q0=makeQuery(id+"F17.imprint","IMPRINT",FACE,{"disambiguationData":[TD([[makeQuery(id+"F17.imprint","IMPRINT",EDGE,{"derivedFrom":makeQuery(id+"F3.opExtrude","CAP_EDGE",EDGE,{"disambiguationData":[OSD([subQ1])],"isStart":false})}),1.0]])]});}
            var Q1;
            {var subQ0=sQuery(id+"F17.wireOp",EDGE,"E78.left");Q1=makeQuery(id+"F17.imprint","IMPRINT",FACE,{"disambiguationData":[TD([[makeQuery(id+"F17.imprint","IMPRINT",EDGE,{"derivedFrom":subQ0}),1.0]])]});}
            var Q2;
            Q2=makeQuery(id+"F17.imprint","IMPRINT",FACE,{"disambiguationData":[TD([[makeQuery(id+"F17.imprint","IMPRINT",EDGE,{"derivedFrom":sQuery(id+"F17.wireOp",EDGE,"E84.top")}),1.0]])]});
            var Q3;
            {var subQ0=sQuery(id+"F17.wireOp",EDGE,"E91.left");Q3=makeQuery(id+"F17.imprint","IMPRINT",FACE,{"disambiguationData":[TD([[makeQuery(id+"F17.imprint","IMPRINT",EDGE,{"derivedFrom":subQ0}),-1.0]])]});}
            var Q4;
            Q4=makeQuery(id+"F17.imprint","IMPRINT",FACE,{"disambiguationData":[TD([[makeQuery(id+"F17.imprint","IMPRINT",EDGE,{"derivedFrom":sQuery(id+"F17.wireOp",EDGE,"E96.top")}),1.0]])]});
            var Q5;
            Q5=makeQuery(id+"F17.imprint","IMPRINT",FACE,{"disambiguationData":[TD([[makeQuery(id+"F17.imprint","IMPRINT",EDGE,{"derivedFrom":sQuery(id+"F17.wireOp",EDGE,"E86.bottom")}),-1.0]])]});
            var Q6;
            {var subQ1=sQuery(id+"F17.wireOp",EDGE,"E93.right");Q6=makeQuery(id+"F17.imprint","IMPRINT",FACE,{"disambiguationData":[TD([[makeQuery(id+"F17.imprint","IMPRINT",EDGE,{"derivedFrom":subQ1}),-1.0]])]});}
            var Q7;
            Q7=makeQuery(id+"F17.imprint","IMPRINT",FACE,{"disambiguationData":[TD([[makeQuery(id+"F17.imprint","IMPRINT",EDGE,{"derivedFrom":sQuery(id+"F17.wireOp",EDGE,"E101.bottom")}),1.0]])]});
            var Q8;
            Q8=makeQuery(id+"F17.imprint","IMPRINT",FACE,{"disambiguationData":[TD([[makeQuery(id+"F17.imprint","IMPRINT",EDGE,{"derivedFrom":sQuery(id+"F17.wireOp",EDGE,"E90.top")}),-1.0]])]});
            extrude(context, id + "F18", {"entities" : qUnion([Q0, Q1, Q2, Q3, Q4, Q5, Q6, Q7, Q8]), "depth" : 15.88 * mm});
        }
        {
            var Q0;
            Q0=makeQuery(id+"F17.imprint","IMPRINT",FACE,{"disambiguationData":[TD([[makeQuery(id+"F17.imprint","IMPRINT",EDGE,{"derivedFrom":sQuery(id+"F17.wireOp",EDGE,"E80.bottom")}),-1.0]])]});
            var Q1;
            Q1=makeQuery(id+"F17.imprint","IMPRINT",FACE,{"disambiguationData":[TD([[makeQuery(id+"F17.imprint","IMPRINT",EDGE,{"derivedFrom":sQuery(id+"F17.wireOp",EDGE,"E94.top")}),1.0]])]});
            var Q2;
            Q2=makeQuery(id+"F17.imprint","IMPRINT",FACE,{"disambiguationData":[TD([[makeQuery(id+"F17.imprint","IMPRINT",EDGE,{"derivedFrom":sQuery(id+"F17.wireOp",EDGE,"E81.bottom")}),-1.0]])]});
            var Q3;
            {var subQ1=sQuery(id+"F17.wireOp",EDGE,"E91.right");Q3=makeQuery(id+"F17.imprint","IMPRINT",FACE,{"disambiguationData":[TD([[makeQuery(id+"F17.imprint","IMPRINT",EDGE,{"derivedFrom":subQ1}),-1.0]])]});}
            var Q4;
            Q4=makeQuery(id+"F17.imprint","IMPRINT",FACE,{"disambiguationData":[TD([[makeQuery(id+"F17.imprint","IMPRINT",EDGE,{"derivedFrom":sQuery(id+"F17.wireOp",EDGE,"E99.bottom")}),1.0]])]});
            var Q5;
            Q5=makeQuery(id+"F17.imprint","IMPRINT",FACE,{"disambiguationData":[TD([[makeQuery(id+"F17.imprint","IMPRINT",EDGE,{"derivedFrom":sQuery(id+"F17.wireOp",EDGE,"E87.bottom")}),-1.0]])]});
            var Q6;
            {var subQ1=sQuery(id+"F17.wireOp",EDGE,"E97.right");Q6=makeQuery(id+"F17.imprint","IMPRINT",FACE,{"disambiguationData":[TD([[makeQuery(id+"F17.imprint","IMPRINT",EDGE,{"derivedFrom":subQ1}),-1.0]])]});}
            extrude(context, id + "F19", {"entities" : qUnion([Q0, Q1, Q2, Q3, Q4, Q5, Q6]), "depth" : 15.88 * mm});
        }
        {
            var Q0;
            {var subQ0=sQuery(id+"F17.wireOp",EDGE,"E80.right");Q0=makeQuery(id+"F17.imprint","IMPRINT",FACE,{"disambiguationData":[TD([[makeQuery(id+"F17.imprint","IMPRINT",EDGE,{"derivedFrom":subQ0}),1.0]])]});}
            var Q1;
            Q1=makeQuery(id+"F17.imprint","IMPRINT",FACE,{"disambiguationData":[TD([[makeQuery(id+"F17.imprint","IMPRINT",EDGE,{"derivedFrom":sQuery(id+"F17.wireOp",EDGE,"E95.top")}),1.0]])]});
            var Q2;
            Q2=makeQuery(id+"F17.imprint","IMPRINT",FACE,{"disambiguationData":[TD([[makeQuery(id+"F17.imprint","IMPRINT",EDGE,{"derivedFrom":sQuery(id+"F17.wireOp",EDGE,"E85.bottom")}),-1.0]])]});
            var Q3;
            {var subQ0=sQuery(id+"F17.wireOp",EDGE,"E92.right");Q3=makeQuery(id+"F17.imprint","IMPRINT",FACE,{"disambiguationData":[TD([[makeQuery(id+"F17.imprint","IMPRINT",EDGE,{"derivedFrom":subQ0}),-1.0]])]});}
            var Q4;
            Q4=makeQuery(id+"F17.imprint","IMPRINT",FACE,{"disambiguationData":[TD([[makeQuery(id+"F17.imprint","IMPRINT",EDGE,{"derivedFrom":sQuery(id+"F17.wireOp",EDGE,"E88.bottom")}),-1.0]])]});
            var Q5;
            Q5=makeQuery(id+"F17.imprint","IMPRINT",FACE,{"disambiguationData":[TD([[makeQuery(id+"F17.imprint","IMPRINT",EDGE,{"derivedFrom":sQuery(id+"F17.wireOp",EDGE,"E100.bottom")}),1.0]])]});
            extrude(context, id + "F20", {"entities" : qUnion([Q0, Q1, Q2, Q3, Q4, Q5]), "depth" : 15.88 * mm});
        }
        {
            var Q0;
            Q0=makeQuery(id+"F3.opExtrude","SWEPT_FACE",FACE,{"disambiguationData":[OSD([sQuery(id+"F2.wireOp",EDGE,"E11.right")])]});
            var sketch = newSketch(context, id + "F21", { "sketchPlane" : qUnion([Q0])});
            skLineSegment(sketch, "E102.0", {"start": v(1828.8, 38.1) * mm, "end": v(1866.9, 38.1) * mm, "construction": true});
            skPoint(sketch, "E103.oppositeSnap0", {"position": v(1847.85, 38.1) * mm});
            skLineSegment(sketch, "E103.bottom", {"start": v(0, 0) * mm, "end": v(1847.85, 0) * mm});
            skLineSegment(sketch, "E103.top", {"start": v(0, 1219.2) * mm, "end": v(1847.85, 1219.2) * mm});
            skLineSegment(sketch, "E103.left", {"start": v(0, 0) * mm, "end": v(0, 1219.2) * mm});
            skLineSegment(sketch, "E103.right", {"start": v(1847.85, 0) * mm, "end": v(1847.85, 1219.2) * mm});
            skLineSegment(sketch, "E104.0", {"start": v(1219.2, 38.1) * mm, "end": v(1257.3, 38.1) * mm, "construction": true});
            skPoint(sketch, "E105.oppositeSnap0", {"position": v(1238.25, 38.1) * mm});
            skLineSegment(sketch, "E105.bottom", {"start": v(0, 1219.2) * mm, "end": v(1238.25, 1219.2) * mm});
            skLineSegment(sketch, "E105.top", {"start": v(0, 2438.4) * mm, "end": v(1238.25, 2438.4) * mm});
            skLineSegment(sketch, "E105.left", {"start": v(0, 1219.2) * mm, "end": v(0, 2438.4) * mm});
            skLineSegment(sketch, "E105.right", {"start": v(1238.25, 1219.2) * mm, "end": v(1238.25, 2438.4) * mm});
            skPoint(sketch, "E106.0", {"position": v(0, 3124.2) * mm});
            skLineSegment(sketch, "E107.bottom", {"start": v(0, 2438.4) * mm, "end": v(1847.85, 2438.4) * mm});
            skLineSegment(sketch, "E107.top", {"start": v(0, 3124.2) * mm, "end": v(1847.85, 3124.2) * mm});
            skLineSegment(sketch, "E107.left", {"start": v(0, 2438.4) * mm, "end": v(0, 3124.2) * mm});
            skLineSegment(sketch, "E107.right", {"start": v(1847.85, 2438.4) * mm, "end": v(1847.85, 3124.2) * mm});
            skLineSegment(sketch, "E108.bottom", {"start": v(1847.85, 0) * mm, "end": v(4286.25, 0) * mm});
            skLineSegment(sketch, "E108.top", {"start": v(1847.85, 1219.2) * mm, "end": v(4286.25, 1219.2) * mm});
            skLineSegment(sketch, "E108.right", {"start": v(4286.25, 0) * mm, "end": v(4286.25, 1219.2) * mm});
            skLineSegment(sketch, "E109.bottom", {"start": v(1238.25, 1219.2) * mm, "end": v(3676.65, 1219.2) * mm});
            skLineSegment(sketch, "E109.top", {"start": v(1238.25, 2438.4) * mm, "end": v(3676.65, 2438.4) * mm});
            skLineSegment(sketch, "E109.right", {"start": v(3676.65, 1219.2) * mm, "end": v(3676.65, 2438.4) * mm});
            skLineSegment(sketch, "E110.bottom", {"start": v(1847.85, 2438.4) * mm, "end": v(4286.25, 2438.4) * mm});
            skLineSegment(sketch, "E110.top", {"start": v(1847.85, 3124.2) * mm, "end": v(4286.25, 3124.2) * mm});
            skLineSegment(sketch, "E110.right", {"start": v(4286.25, 2438.4) * mm, "end": v(4286.25, 3124.2) * mm});
            skLineSegment(sketch, "E111.bottom", {"start": v(4286.25, 0) * mm, "end": v(6724.65, 0) * mm});
            skLineSegment(sketch, "E111.top", {"start": v(4286.25, 1219.2) * mm, "end": v(6724.65, 1219.2) * mm});
            skLineSegment(sketch, "E111.right", {"start": v(6724.65, 0) * mm, "end": v(6724.65, 1219.2) * mm});
            skLineSegment(sketch, "E112.bottom", {"start": v(3676.65, 2438.4) * mm, "end": v(6115.05, 2438.4) * mm});
            skLineSegment(sketch, "E112.top", {"start": v(3676.65, 1219.2) * mm, "end": v(6115.05, 1219.2) * mm});
            skLineSegment(sketch, "E112.left", {"start": v(3676.65, 2438.4) * mm, "end": v(3676.65, 1219.2) * mm});
            skLineSegment(sketch, "E112.right", {"start": v(6115.05, 2438.4) * mm, "end": v(6115.05, 1219.2) * mm});
            skLineSegment(sketch, "E113.bottom", {"start": v(4286.25, 3124.2) * mm, "end": v(6724.65, 3124.2) * mm});
            skLineSegment(sketch, "E113.top", {"start": v(4286.25, 2438.4) * mm, "end": v(6724.65, 2438.4) * mm});
            skLineSegment(sketch, "E113.left", {"start": v(4286.25, 3124.2) * mm, "end": v(4286.25, 2438.4) * mm});
            skLineSegment(sketch, "E113.right", {"start": v(6724.65, 3124.2) * mm, "end": v(6724.65, 2438.4) * mm});
            skPoint(sketch, "E114.0", {"position": v(8550.27, 0) * mm});
            skLineSegment(sketch, "E115.bottom", {"start": v(6724.65, 1219.2) * mm, "end": v(8550.27, 1219.2) * mm});
            skLineSegment(sketch, "E115.top", {"start": v(6724.65, 0) * mm, "end": v(8550.27, 0) * mm});
            skLineSegment(sketch, "E115.left", {"start": v(6724.65, 1219.2) * mm, "end": v(6724.65, 0) * mm});
            skLineSegment(sketch, "E115.right", {"start": v(8550.27, 1219.2) * mm, "end": v(8550.27, 0) * mm});
            skLineSegment(sketch, "E116.bottom", {"start": v(6115.05, 2438.4) * mm, "end": v(8550.27, 2438.4) * mm});
            skLineSegment(sketch, "E116.top", {"start": v(6115.05, 1219.2) * mm, "end": v(8550.27, 1219.2) * mm});
            skLineSegment(sketch, "E116.right", {"start": v(8550.27, 2438.4) * mm, "end": v(8550.27, 1219.2) * mm});
            skLineSegment(sketch, "E117.bottom", {"start": v(6724.65, 3124.2) * mm, "end": v(8550.27, 3124.2) * mm});
            skLineSegment(sketch, "E117.top", {"start": v(6724.65, 2438.4) * mm, "end": v(8550.27, 2438.4) * mm});
            skLineSegment(sketch, "E117.right", {"start": v(8550.27, 3124.2) * mm, "end": v(8550.27, 2438.4) * mm});
            skSolve(sketch);
        }
        {
            var Q0;
            {var subQ1=sQuery(id+"F21.wireOp",EDGE,"E105.bottom");Q0=makeQuery(id+"F21.imprint","IMPRINT",FACE,{"disambiguationData":[TD([[makeQuery(id+"F21.imprint","IMPRINT",EDGE,{"derivedFrom":subQ1}),-1.0]])]});}
            var Q1;
            Q1=makeQuery(id+"F21.imprint","IMPRINT",FACE,{"disambiguationData":[TD([[makeQuery(id+"F21.imprint","IMPRINT",EDGE,{"derivedFrom":sQuery(id+"F21.wireOp",EDGE,"E107.bottom")}),1.0]])]});
            var Q2;
            Q2=makeQuery(id+"F21.imprint","IMPRINT",FACE,{"disambiguationData":[TD([[makeQuery(id+"F21.imprint","IMPRINT",EDGE,{"derivedFrom":sQuery(id+"F21.wireOp",EDGE,"E111.bottom")}),1.0]])]});
            var Q3;
            Q3=makeQuery(id+"F21.imprint","IMPRINT",FACE,{"disambiguationData":[TD([[makeQuery(id+"F21.imprint","IMPRINT",EDGE,{"derivedFrom":sQuery(id+"F21.wireOp",EDGE,"E113.bottom")}),-1.0]])]});
            var Q4;
            {var subQ0=sQuery(id+"F21.wireOp",EDGE,"E103.bottom");Q4=makeQuery(id+"F21.imprint","IMPRINT",FACE,{"disambiguationData":[TD([[makeQuery(id+"F21.imprint","IMPRINT",EDGE,{"derivedFrom":subQ0}),-1.0]])]});}
            extrude(context, id + "F22", {"entities" : qUnion([Q0, Q1, Q2, Q3, Q4]), "depth" : 15.88 * mm});
        }
        {
            var Q0;
            Q0=makeQuery(id+"F21.imprint","IMPRINT",FACE,{"disambiguationData":[TD([[makeQuery(id+"F21.imprint","IMPRINT",EDGE,{"derivedFrom":sQuery(id+"F21.wireOp",EDGE,"E109.top")}),-1.0]])]});
            var Q1;
            Q1=makeQuery(id+"F21.imprint","IMPRINT",FACE,{"disambiguationData":[TD([[makeQuery(id+"F21.imprint","IMPRINT",EDGE,{"derivedFrom":sQuery(id+"F21.wireOp",EDGE,"E116.bottom")}),-1.0]])]});
            extrude(context, id + "F23", {"entities" : qUnion([Q0, Q1]), "depth" : 15.88 * mm});
        }
        {
            var Q0;
            Q0=makeQuery(id+"F21.imprint","IMPRINT",FACE,{"disambiguationData":[TD([[makeQuery(id+"F21.imprint","IMPRINT",EDGE,{"derivedFrom":sQuery(id+"F21.wireOp",EDGE,"E105.bottom")}),1.0]])]});
            var Q1;
            Q1=makeQuery(id+"F21.imprint","IMPRINT",FACE,{"disambiguationData":[TD([[makeQuery(id+"F21.imprint","IMPRINT",EDGE,{"derivedFrom":sQuery(id+"F21.wireOp",EDGE,"E112.bottom")}),-1.0]])]});
            extrude(context, id + "F24", {"entities" : qUnion([Q0, Q1]), "depth" : 15.88 * mm});
        }
        {
            var Q0;
            Q0=makeQuery(id+"F21.imprint","IMPRINT",FACE,{"disambiguationData":[TD([[makeQuery(id+"F21.imprint","IMPRINT",EDGE,{"derivedFrom":sQuery(id+"F21.wireOp",EDGE,"E110.bottom")}),1.0]])]});
            var Q1;
            {var subQ9=sQuery(id+"F21.wireOp",EDGE,"E108.right");Q1=makeQuery(id+"F21.imprint","IMPRINT",FACE,{"disambiguationData":[TD([[makeQuery(id+"F21.imprint","IMPRINT",EDGE,{"derivedFrom":subQ9}),1.0]])]});}
            var Q2;
            Q2=makeQuery(id+"F21.imprint","IMPRINT",FACE,{"disambiguationData":[TD([[makeQuery(id+"F21.imprint","IMPRINT",EDGE,{"derivedFrom":sQuery(id+"F21.wireOp",EDGE,"E115.top")}),1.0]])]});
            var Q3;
            Q3=makeQuery(id+"F21.imprint","IMPRINT",FACE,{"disambiguationData":[TD([[makeQuery(id+"F21.imprint","IMPRINT",EDGE,{"derivedFrom":sQuery(id+"F21.wireOp",EDGE,"E117.bottom")}),-1.0]])]});
            var Q4;
            {var subQ1=sQuery(id+"F2.wireOp",EDGE,"E11.right");var subQ2=makeQuery(id+"F3.opExtrude","SWEPT_EDGE",EDGE,{"disambiguationData":[OSD([sQuery(id+"F2.wireOp",EDGE,"E10.right"),sQuery(id+"F2.wireOp",EDGE,"E10.top"),subQ1])]});Q4=makeQuery(id+"F21.imprint","IMPRINT",FACE,{"disambiguationData":[TD([[makeQuery(id+"F21.imprint","IMPRINT",EDGE,{"derivedFrom":subQ2}),-1.0]])]});}
            extrude(context, id + "F25", {"entities" : qUnion([Q0, Q1, Q2, Q3, Q4]), "depth" : 15.88 * mm});
        }
        {
            var Q0;
            Q0=makeQuery(id+"F3.opExtrude","SWEPT_FACE",FACE,{"disambiguationData":[OSD([sQuery(id+"F2.wireOp",EDGE,"E1.bottom")])]});
            var sketch = newSketch(context, id + "F26", { "sketchPlane" : qUnion([Q0])});
            skPoint(sketch, "E118.0", {"position": v(-15.88, 0) * mm});
            skPoint(sketch, "E119.0", {"position": v(-15.88, 3124.2) * mm});
            skLineSegment(sketch, "E120.bottom", {"start": v(-15.87, 0) * mm, "end": v(1987.55, 0) * mm});
            skLineSegment(sketch, "E120.top", {"start": v(-15.88, 1219.2) * mm, "end": v(1987.55, 1219.2) * mm});
            skLineSegment(sketch, "E120.left", {"start": v(-15.88, 0) * mm, "end": v(-15.88, 1219.2) * mm});
            skLineSegment(sketch, "E120.right", {"start": v(1987.55, 0) * mm, "end": v(1987.55, 1219.2) * mm});
            skLineSegment(sketch, "E121.bottom", {"start": v(-15.88, 1219.2) * mm, "end": v(768.35, 1219.2) * mm});
            skLineSegment(sketch, "E121.top", {"start": v(-15.88, 2438.4) * mm, "end": v(768.35, 2438.4) * mm});
            skLineSegment(sketch, "E121.left", {"start": v(-15.88, 1219.2) * mm, "end": v(-15.88, 2438.4) * mm});
            skLineSegment(sketch, "E121.right", {"start": v(768.35, 1219.2) * mm, "end": v(768.35, 2438.4) * mm});
            skLineSegment(sketch, "E122.bottom", {"start": v(-15.88, 2438.4) * mm, "end": v(1987.55, 2438.4) * mm});
            skLineSegment(sketch, "E122.top", {"start": v(-15.88, 3124.2) * mm, "end": v(1987.55, 3124.2) * mm});
            skLineSegment(sketch, "E122.left", {"start": v(-15.88, 2438.4) * mm, "end": v(-15.88, 3124.2) * mm});
            skLineSegment(sketch, "E122.right", {"start": v(1987.55, 2438.4) * mm, "end": v(1987.55, 3124.2) * mm});
            skLineSegment(sketch, "E123.bottom", {"start": v(1987.55, 1219.2) * mm, "end": v(4425.95, 1219.2) * mm});
            skLineSegment(sketch, "E123.top", {"start": v(1987.55, 0) * mm, "end": v(4425.95, 0) * mm});
            skLineSegment(sketch, "E123.left", {"start": v(1987.55, 1219.2) * mm, "end": v(1987.55, 0) * mm});
            skLineSegment(sketch, "E123.right", {"start": v(4425.95, 1219.2) * mm, "end": v(4425.95, 0) * mm});
            skLineSegment(sketch, "E124.bottom", {"start": v(768.35, 1219.2) * mm, "end": v(3206.75, 1219.2) * mm});
            skLineSegment(sketch, "E124.top", {"start": v(768.35, 2438.4) * mm, "end": v(3206.75, 2438.4) * mm});
            skLineSegment(sketch, "E124.right", {"start": v(3206.75, 1219.2) * mm, "end": v(3206.75, 2438.4) * mm});
            skLineSegment(sketch, "E125.bottom", {"start": v(1987.55, 3124.2) * mm, "end": v(4425.95, 3124.2) * mm});
            skLineSegment(sketch, "E125.top", {"start": v(1987.55, 2438.4) * mm, "end": v(4425.95, 2438.4) * mm});
            skLineSegment(sketch, "E125.left", {"start": v(1987.55, 3124.2) * mm, "end": v(1987.55, 2438.4) * mm});
            skLineSegment(sketch, "E125.right", {"start": v(4425.95, 3124.2) * mm, "end": v(4425.95, 2438.4) * mm});
            skLineSegment(sketch, "E126.bottom", {"start": v(4425.95, 0) * mm, "end": v(6864.35, 0) * mm});
            skLineSegment(sketch, "E126.top", {"start": v(4425.95, 1219.2) * mm, "end": v(6864.35, 1219.2) * mm});
            skLineSegment(sketch, "E126.left", {"start": v(4425.95, 0) * mm, "end": v(4425.95, 1219.2) * mm});
            skLineSegment(sketch, "E126.right", {"start": v(6864.35, 0) * mm, "end": v(6864.35, 1219.2) * mm});
            skLineSegment(sketch, "E127.bottom", {"start": v(3206.75, 2438.4) * mm, "end": v(5645.15, 2438.4) * mm});
            skLineSegment(sketch, "E127.top", {"start": v(3206.75, 1219.2) * mm, "end": v(5645.15, 1219.2) * mm});
            skLineSegment(sketch, "E127.left", {"start": v(3206.75, 2438.4) * mm, "end": v(3206.75, 1219.2) * mm});
            skLineSegment(sketch, "E127.right", {"start": v(5645.15, 2438.4) * mm, "end": v(5645.15, 1219.2) * mm});
            skLineSegment(sketch, "E128.bottom", {"start": v(4425.95, 3124.2) * mm, "end": v(6864.35, 3124.2) * mm});
            skLineSegment(sketch, "E128.top", {"start": v(4425.95, 2438.4) * mm, "end": v(6864.35, 2438.4) * mm});
            skLineSegment(sketch, "E128.right", {"start": v(6864.35, 3124.2) * mm, "end": v(6864.35, 2438.4) * mm});
            skLineSegment(sketch, "E129.bottom", {"start": v(6864.35, 1219.2) * mm, "end": v(9302.75, 1219.2) * mm});
            skLineSegment(sketch, "E129.top", {"start": v(6864.35, 0) * mm, "end": v(9302.75, 0) * mm});
            skLineSegment(sketch, "E129.left", {"start": v(6864.35, 1219.2) * mm, "end": v(6864.35, 0) * mm});
            skLineSegment(sketch, "E129.right", {"start": v(9302.75, 1219.2) * mm, "end": v(9302.75, 0) * mm});
            skLineSegment(sketch, "E130.bottom", {"start": v(5645.15, 2438.4) * mm, "end": v(8083.55, 2438.4) * mm});
            skLineSegment(sketch, "E130.top", {"start": v(5645.15, 1219.2) * mm, "end": v(8083.55, 1219.2) * mm});
            skLineSegment(sketch, "E130.right", {"start": v(8083.55, 2438.4) * mm, "end": v(8083.55, 1219.2) * mm});
            skLineSegment(sketch, "E131.bottom", {"start": v(9302.75, 0) * mm, "end": v(11741.15, 0) * mm});
            skLineSegment(sketch, "E131.top", {"start": v(9302.75, 1219.2) * mm, "end": v(11741.15, 1219.2) * mm});
            skLineSegment(sketch, "E131.left", {"start": v(9302.75, 0) * mm, "end": v(9302.75, 1219.2) * mm});
            skLineSegment(sketch, "E131.right", {"start": v(11741.15, 0) * mm, "end": v(11741.15, 1219.2) * mm});
            skLineSegment(sketch, "E132.bottom", {"start": v(8083.55, 1219.2) * mm, "end": v(10521.95, 1219.2) * mm});
            skLineSegment(sketch, "E132.top", {"start": v(8083.55, 2438.4) * mm, "end": v(10521.95, 2438.4) * mm});
            skLineSegment(sketch, "E132.left", {"start": v(8083.55, 1219.2) * mm, "end": v(8083.55, 2438.4) * mm});
            skLineSegment(sketch, "E132.right", {"start": v(10521.95, 1219.2) * mm, "end": v(10521.95, 2438.4) * mm});
            skLineSegment(sketch, "E133.bottom", {"start": v(6864.35, 3124.2) * mm, "end": v(9302.75, 3124.2) * mm});
            skLineSegment(sketch, "E133.top", {"start": v(6864.35, 2438.4) * mm, "end": v(9302.75, 2438.4) * mm});
            skLineSegment(sketch, "E133.right", {"start": v(9302.75, 3124.2) * mm, "end": v(9302.75, 2438.4) * mm});
            skLineSegment(sketch, "E134.bottom", {"start": v(11741.15, 0) * mm, "end": v(14179.55, 0) * mm});
            skLineSegment(sketch, "E134.top", {"start": v(11741.15, 1219.2) * mm, "end": v(14179.55, 1219.2) * mm});
            skLineSegment(sketch, "E134.right", {"start": v(14179.55, 0) * mm, "end": v(14179.55, 1219.2) * mm});
            skLineSegment(sketch, "E135.bottom", {"start": v(10521.95, 2438.4) * mm, "end": v(12960.35, 2438.4) * mm});
            skLineSegment(sketch, "E135.top", {"start": v(10521.95, 1219.2) * mm, "end": v(12960.35, 1219.2) * mm});
            skLineSegment(sketch, "E135.left", {"start": v(10521.95, 2438.4) * mm, "end": v(10521.95, 1219.2) * mm});
            skLineSegment(sketch, "E135.right", {"start": v(12960.35, 2438.4) * mm, "end": v(12960.35, 1219.2) * mm});
            skLineSegment(sketch, "E136.bottom", {"start": v(9302.75, 3124.2) * mm, "end": v(11741.15, 3124.2) * mm});
            skLineSegment(sketch, "E136.top", {"start": v(9302.75, 2438.4) * mm, "end": v(11741.15, 2438.4) * mm});
            skLineSegment(sketch, "E136.right", {"start": v(11741.15, 3124.2) * mm, "end": v(11741.15, 2438.4) * mm});
            skPoint(sketch, "E137.0", {"position": v(14646.28, 0) * mm});
            skPoint(sketch, "E138.0", {"position": v(14646.28, 3124.2) * mm});
            skLineSegment(sketch, "E139.bottom", {"start": v(14179.55, 1219.2) * mm, "end": v(14646.28, 1219.2) * mm});
            skLineSegment(sketch, "E139.top", {"start": v(14179.55, 0) * mm, "end": v(14646.28, 0) * mm});
            skLineSegment(sketch, "E139.left", {"start": v(14179.55, 1219.2) * mm, "end": v(14179.55, 0) * mm});
            skLineSegment(sketch, "E139.right", {"start": v(14646.28, 1219.2) * mm, "end": v(14646.28, 0) * mm});
            skLineSegment(sketch, "E140.bottom", {"start": v(12960.35, 2438.4) * mm, "end": v(14646.28, 2438.4) * mm});
            skLineSegment(sketch, "E140.top", {"start": v(12960.35, 1219.2) * mm, "end": v(14646.28, 1219.2) * mm});
            skLineSegment(sketch, "E140.right", {"start": v(14646.28, 2438.4) * mm, "end": v(14646.28, 1219.2) * mm});
            skLineSegment(sketch, "E141.bottom", {"start": v(11741.15, 3124.2) * mm, "end": v(14179.55, 3124.2) * mm});
            skLineSegment(sketch, "E141.top", {"start": v(11741.15, 2438.4) * mm, "end": v(14179.55, 2438.4) * mm});
            skLineSegment(sketch, "E141.right", {"start": v(14179.55, 3124.2) * mm, "end": v(14179.55, 2438.4) * mm});
            skLineSegment(sketch, "E142.bottom", {"start": v(14179.55, 3124.2) * mm, "end": v(14646.28, 3124.2) * mm});
            skLineSegment(sketch, "E142.top", {"start": v(14179.55, 2438.4) * mm, "end": v(14646.28, 2438.4) * mm});
            skLineSegment(sketch, "E142.right", {"start": v(14646.28, 3124.2) * mm, "end": v(14646.28, 2438.4) * mm});
            skSolve(sketch);
        }
        {
            var Q0;
            {var subQ2=sQuery(id+"F26.wireOp",EDGE,"E120.left");Q0=makeQuery(id+"F26.imprint","IMPRINT",FACE,{"disambiguationData":[TD([[makeQuery(id+"F26.imprint","IMPRINT",EDGE,{"derivedFrom":subQ2}),-1.0]])]});}
            var Q1;
            Q1=makeQuery(id+"F26.imprint","IMPRINT",FACE,{"disambiguationData":[TD([[makeQuery(id+"F26.imprint","IMPRINT",EDGE,{"derivedFrom":sQuery(id+"F26.wireOp",EDGE,"E122.bottom")}),1.0]])]});
            var Q2;
            Q2=makeQuery(id+"F26.imprint","IMPRINT",FACE,{"disambiguationData":[TD([[makeQuery(id+"F26.imprint","IMPRINT",EDGE,{"derivedFrom":sQuery(id+"F26.wireOp",EDGE,"E126.bottom")}),1.0]])]});
            var Q3;
            Q3=makeQuery(id+"F26.imprint","IMPRINT",FACE,{"disambiguationData":[TD([[makeQuery(id+"F26.imprint","IMPRINT",EDGE,{"derivedFrom":sQuery(id+"F26.wireOp",EDGE,"E128.bottom")}),-1.0]])]});
            var Q4;
            Q4=makeQuery(id+"F26.imprint","IMPRINT",FACE,{"disambiguationData":[TD([[makeQuery(id+"F26.imprint","IMPRINT",EDGE,{"derivedFrom":sQuery(id+"F26.wireOp",EDGE,"E136.bottom")}),-1.0]])]});
            var Q5;
            Q5=makeQuery(id+"F26.imprint","IMPRINT",FACE,{"disambiguationData":[TD([[makeQuery(id+"F26.imprint","IMPRINT",EDGE,{"derivedFrom":sQuery(id+"F26.wireOp",EDGE,"E131.bottom")}),1.0]])]});
            var Q6;
            Q6=makeQuery(id+"F26.imprint","IMPRINT",FACE,{"disambiguationData":[TD([[makeQuery(id+"F26.imprint","IMPRINT",EDGE,{"derivedFrom":sQuery(id+"F26.wireOp",EDGE,"E139.top")}),1.0]])]});
            var Q7;
            Q7=makeQuery(id+"F26.imprint","IMPRINT",FACE,{"disambiguationData":[TD([[makeQuery(id+"F26.imprint","IMPRINT",EDGE,{"derivedFrom":sQuery(id+"F26.wireOp",EDGE,"E142.bottom")}),-1.0]])]});
            extrude(context, id + "F27", {"entities" : qUnion([Q0, Q1, Q2, Q3, Q4, Q5, Q6, Q7]), "depth" : 15.88 * mm});
        }
        {
            var Q0;
            Q0=makeQuery(id+"F26.imprint","IMPRINT",FACE,{"disambiguationData":[TD([[makeQuery(id+"F26.imprint","IMPRINT",EDGE,{"derivedFrom":sQuery(id+"F26.wireOp",EDGE,"E121.bottom")}),1.0]])]});
            var Q1;
            Q1=makeQuery(id+"F26.imprint","IMPRINT",FACE,{"disambiguationData":[TD([[makeQuery(id+"F26.imprint","IMPRINT",EDGE,{"derivedFrom":sQuery(id+"F26.wireOp",EDGE,"E127.bottom")}),-1.0]])]});
            var Q2;
            {var subQ1=sQuery(id+"F26.wireOp",EDGE,"E132.left");Q2=makeQuery(id+"F26.imprint","IMPRINT",FACE,{"disambiguationData":[TD([[makeQuery(id+"F26.imprint","IMPRINT",EDGE,{"derivedFrom":subQ1}),-1.0]])]});}
            var Q3;
            {var subQ1=sQuery(id+"F26.wireOp",EDGE,"E135.right");Q3=makeQuery(id+"F26.imprint","IMPRINT",FACE,{"disambiguationData":[TD([[makeQuery(id+"F26.imprint","IMPRINT",EDGE,{"derivedFrom":subQ1}),1.0]])]});}
            extrude(context, id + "F28", {"entities" : qUnion([Q0, Q1, Q2, Q3]), "depth" : 15.88 * mm});
        }
        {
            var Q0;
            Q0=makeQuery(id+"F26.imprint","IMPRINT",FACE,{"disambiguationData":[TD([[makeQuery(id+"F26.imprint","IMPRINT",EDGE,{"derivedFrom":sQuery(id+"F26.wireOp",EDGE,"E125.bottom")}),-1.0]])]});
            var Q1;
            Q1=makeQuery(id+"F26.imprint","IMPRINT",FACE,{"disambiguationData":[TD([[makeQuery(id+"F26.imprint","IMPRINT",EDGE,{"derivedFrom":sQuery(id+"F26.wireOp",EDGE,"E123.top")}),1.0]])]});
            var Q2;
            Q2=makeQuery(id+"F26.imprint","IMPRINT",FACE,{"disambiguationData":[TD([[makeQuery(id+"F26.imprint","IMPRINT",EDGE,{"derivedFrom":sQuery(id+"F26.wireOp",EDGE,"E129.top")}),1.0]])]});
            var Q3;
            Q3=makeQuery(id+"F26.imprint","IMPRINT",FACE,{"disambiguationData":[TD([[makeQuery(id+"F26.imprint","IMPRINT",EDGE,{"derivedFrom":sQuery(id+"F26.wireOp",EDGE,"E133.bottom")}),-1.0]])]});
            var Q4;
            Q4=makeQuery(id+"F26.imprint","IMPRINT",FACE,{"disambiguationData":[TD([[makeQuery(id+"F26.imprint","IMPRINT",EDGE,{"derivedFrom":sQuery(id+"F26.wireOp",EDGE,"E141.bottom")}),-1.0]])]});
            var Q5;
            Q5=makeQuery(id+"F26.imprint","IMPRINT",FACE,{"disambiguationData":[TD([[makeQuery(id+"F26.imprint","IMPRINT",EDGE,{"derivedFrom":sQuery(id+"F26.wireOp",EDGE,"E134.bottom")}),1.0]])]});
            extrude(context, id + "F29", {"entities" : qUnion([Q0, Q1, Q2, Q3, Q4, Q5]), "depth" : 15.88 * mm});
        }
        {
            var Q0;
            Q0=makeQuery(id+"F26.imprint","IMPRINT",FACE,{"disambiguationData":[TD([[makeQuery(id+"F26.imprint","IMPRINT",EDGE,{"derivedFrom":sQuery(id+"F26.wireOp",EDGE,"E124.top")}),-1.0]])]});
            var Q1;
            {var subQ4=sQuery(id+"F26.wireOp",EDGE,"E130.bottom");Q1=makeQuery(id+"F26.imprint","IMPRINT",FACE,{"disambiguationData":[TD([[makeQuery(id+"F26.imprint","IMPRINT",EDGE,{"derivedFrom":subQ4}),-1.0]])]});}
            var Q2;
            {var subQ1=sQuery(id+"F26.wireOp",EDGE,"E135.left");Q2=makeQuery(id+"F26.imprint","IMPRINT",FACE,{"disambiguationData":[TD([[makeQuery(id+"F26.imprint","IMPRINT",EDGE,{"derivedFrom":subQ1}),1.0]])]});}
            extrude(context, id + "F30", {"entities" : qUnion([Q0, Q1, Q2]), "depth" : 15.88 * mm});
        }
        {
            var Q0;
            Q0=makeQuery(id+"F3.opExtrude","CAP_FACE",FACE,{"disambiguationData":[OSD([sQuery(id+"F2.wireOp",EDGE,"E7.top"),sQuery(id+"F2.wireOp",EDGE,"E8.top"),sQuery(id+"F2.wireOp",EDGE,"E8.left"),sQuery(id+"F2.wireOp",EDGE,"E8.right")])],"isStart":false});
            var sketch = newSketch(context, id + "F31", { "sketchPlane" : qUnion([Q0])});
            skLineSegment(sketch, "E143.0", {"start": v(0, 8534.4) * mm, "end": v(139.7, 8534.4) * mm, "construction": true});
            skLineSegment(sketch, "E144", {"start": v(69.85, 8534.4) * mm, "end": v(69.85, 8280.4) * mm, "construction": true});
            skCircle(sketch, "E145", {"center": v(69.85, 8280.4) * mm, "radius": 9.53 * mm});
            skLineSegment(sketch, "E146.0", {"start": v(0, 6096) * mm, "end": v(139.7, 6096) * mm, "construction": true});
            skLineSegment(sketch, "E147", {"start": v(69.85, 6096) * mm, "end": v(69.85, 6350) * mm, "construction": true});
            skCircle(sketch, "E148", {"center": v(69.85, 6350) * mm, "radius": 9.53 * mm});
            skLineSegment(sketch, "E149", {"start": v(69.85, 6096) * mm, "end": v(69.85, 5842) * mm, "construction": true});
            skCircle(sketch, "E150", {"center": v(69.85, 5842) * mm, "radius": 9.53 * mm});
            skLineSegment(sketch, "E151.0", {"start": v(139.7, 3048) * mm, "end": v(0, 3048) * mm, "construction": true});
            skLineSegment(sketch, "E152.0", {"start": v(0, 0) * mm, "end": v(139.7, 0) * mm, "construction": true});
            skLineSegment(sketch, "E153", {"start": v(69.85, 3048) * mm, "end": v(69.85, 3302) * mm, "construction": true});
            skLineSegment(sketch, "E154", {"start": v(69.85, 3048) * mm, "end": v(69.85, 2794) * mm, "construction": true});
            skCircle(sketch, "E155", {"center": v(69.85, 3302) * mm, "radius": 9.53 * mm});
            skCircle(sketch, "E156", {"center": v(69.85, 2794) * mm, "radius": 9.52 * mm});
            skLineSegment(sketch, "E157", {"start": v(69.85, 0) * mm, "end": v(69.85, 254) * mm, "construction": true});
            skCircle(sketch, "E158", {"center": v(69.85, 254) * mm, "radius": 9.53 * mm});
            skLineSegment(sketch, "E159.0", {"start": v(139.7, 139.7) * mm, "end": v(139.7, 0) * mm, "construction": true});
            skLineSegment(sketch, "E160.0", {"start": v(2298.7, 139.7) * mm, "end": v(2298.7, 0) * mm, "construction": true});
            skLineSegment(sketch, "E161.0", {"start": v(5346.7, 139.7) * mm, "end": v(5346.7, 0) * mm, "construction": true});
            skLineSegment(sketch, "E162.0", {"start": v(8394.7, 139.7) * mm, "end": v(8394.7, 0) * mm, "construction": true});
            skLineSegment(sketch, "E163.0", {"start": v(11442.7, 139.7) * mm, "end": v(11442.7, 0) * mm, "construction": true});
            skLineSegment(sketch, "E164.0", {"start": v(14490.7, 0) * mm, "end": v(14490.7, 139.7) * mm, "construction": true});
            skLineSegment(sketch, "E165.0", {"start": v(14490.7, 0) * mm, "end": v(14630.4, 0) * mm, "construction": true});
            skLineSegment(sketch, "E166.0", {"start": v(14490.7, 2298.7) * mm, "end": v(14630.4, 2298.7) * mm, "construction": true});
            skLineSegment(sketch, "E167.0", {"start": v(14490.7, 5346.7) * mm, "end": v(14630.4, 5346.7) * mm, "construction": true});
            skLineSegment(sketch, "E168.0", {"start": v(14630.4, 8394.7) * mm, "end": v(14490.7, 8394.7) * mm, "construction": true});
            skLineSegment(sketch, "E169.0", {"start": v(14630.4, 8394.7) * mm, "end": v(14630.4, 8534.4) * mm, "construction": true});
            skLineSegment(sketch, "E170.0", {"start": v(12331.7, 8394.7) * mm, "end": v(12331.7, 8534.4) * mm, "construction": true});
            skLineSegment(sketch, "E171.0", {"start": v(9283.7, 8394.7) * mm, "end": v(9283.7, 8534.4) * mm, "construction": true});
            skLineSegment(sketch, "E172.0", {"start": v(6235.7, 8394.7) * mm, "end": v(6235.7, 8534.4) * mm, "construction": true});
            skLineSegment(sketch, "E173.0", {"start": v(3187.7, 8394.7) * mm, "end": v(3187.7, 8534.4) * mm, "construction": true});
            skLineSegment(sketch, "E174.0", {"start": v(139.7, 8394.7) * mm, "end": v(139.7, 8534.4) * mm, "construction": true});
            skLineSegment(sketch, "E175", {"start": v(139.7, 69.85) * mm, "end": v(393.7, 69.85) * mm, "construction": true});
            skLineSegment(sketch, "E176", {"start": v(2298.7, 69.85) * mm, "end": v(2070.1, 69.85) * mm, "construction": true});
            skLineSegment(sketch, "E177", {"start": v(2298.7, 69.85) * mm, "end": v(2527.3, 69.85) * mm, "construction": true});
            skLineSegment(sketch, "E178", {"start": v(5346.7, 69.85) * mm, "end": v(5118.1, 69.85) * mm, "construction": true});
            skLineSegment(sketch, "E179", {"start": v(5346.7, 69.85) * mm, "end": v(5575.3, 69.85) * mm, "construction": true});
            skLineSegment(sketch, "E180", {"start": v(8394.7, 69.85) * mm, "end": v(8166.1, 69.85) * mm, "construction": true});
            skLineSegment(sketch, "E181", {"start": v(8394.7, 69.85) * mm, "end": v(8623.3, 69.85) * mm, "construction": true});
            skLineSegment(sketch, "E182", {"start": v(11442.7, 69.85) * mm, "end": v(11214.1, 69.85) * mm, "construction": true});
            skLineSegment(sketch, "E183", {"start": v(11442.7, 69.85) * mm, "end": v(11671.3, 69.85) * mm, "construction": true});
            skLineSegment(sketch, "E184", {"start": v(14490.7, 69.85) * mm, "end": v(14262.1, 69.85) * mm, "construction": true});
            skLineSegment(sketch, "E185", {"start": v(14560.55, 0) * mm, "end": v(14560.55, 254) * mm, "construction": true});
            skLineSegment(sketch, "E186", {"start": v(14560.55, 2298.7) * mm, "end": v(14560.55, 2044.7) * mm, "construction": true});
            skLineSegment(sketch, "E187", {"start": v(14560.55, 2298.7) * mm, "end": v(14560.55, 2603.5) * mm, "construction": true});
            skLineSegment(sketch, "E188", {"start": v(14560.55, 5346.7) * mm, "end": v(14560.55, 5092.7) * mm, "construction": true});
            skLineSegment(sketch, "E189", {"start": v(14560.55, 5346.7) * mm, "end": v(14560.55, 5651.5) * mm, "construction": true});
            skLineSegment(sketch, "E190", {"start": v(14560.55, 8394.7) * mm, "end": v(14560.55, 8140.7) * mm, "construction": true});
            skLineSegment(sketch, "E191", {"start": v(14630.4, 8464.55) * mm, "end": v(14376.4, 8464.55) * mm, "construction": true});
            skLineSegment(sketch, "E192", {"start": v(9283.7, 8464.55) * mm, "end": v(9029.7, 8464.55) * mm, "construction": true});
            skLineSegment(sketch, "E193", {"start": v(9283.7, 8464.55) * mm, "end": v(9537.7, 8464.55) * mm, "construction": true});
            skLineSegment(sketch, "E194", {"start": v(6235.7, 8464.55) * mm, "end": v(5981.7, 8464.55) * mm, "construction": true});
            skLineSegment(sketch, "E195", {"start": v(6235.7, 8464.55) * mm, "end": v(6489.7, 8464.55) * mm, "construction": true});
            skLineSegment(sketch, "E196", {"start": v(3187.7, 8464.55) * mm, "end": v(2933.7, 8464.55) * mm, "construction": true});
            skLineSegment(sketch, "E197", {"start": v(3187.7, 8464.55) * mm, "end": v(3441.7, 8464.55) * mm, "construction": true});
            skLineSegment(sketch, "E198", {"start": v(139.7, 8464.55) * mm, "end": v(393.7, 8464.55) * mm, "construction": true});
            skCircle(sketch, "E199", {"center": v(393.7, 69.85) * mm, "radius": 9.53 * mm});
            skCircle(sketch, "E200", {"center": v(2070.1, 69.85) * mm, "radius": 9.53 * mm});
            skCircle(sketch, "E201", {"center": v(2527.3, 69.85) * mm, "radius": 9.53 * mm});
            skCircle(sketch, "E202", {"center": v(5118.1, 69.85) * mm, "radius": 9.53 * mm});
            skCircle(sketch, "E203", {"center": v(5575.3, 69.85) * mm, "radius": 9.53 * mm});
            skCircle(sketch, "E204", {"center": v(8166.1, 69.85) * mm, "radius": 9.53 * mm});
            skCircle(sketch, "E205", {"center": v(8623.3, 69.85) * mm, "radius": 9.53 * mm});
            skCircle(sketch, "E206", {"center": v(11214.1, 69.85) * mm, "radius": 9.53 * mm});
            skCircle(sketch, "E207", {"center": v(11671.3, 69.85) * mm, "radius": 9.53 * mm});
            skCircle(sketch, "E208", {"center": v(14262.1, 69.85) * mm, "radius": 9.53 * mm});
            skCircle(sketch, "E209", {"center": v(14560.55, 254) * mm, "radius": 9.53 * mm});
            skCircle(sketch, "E210", {"center": v(14560.55, 2044.7) * mm, "radius": 9.53 * mm});
            skCircle(sketch, "E211", {"center": v(14560.55, 2603.5) * mm, "radius": 9.53 * mm});
            skCircle(sketch, "E212", {"center": v(14560.55, 5651.5) * mm, "radius": 9.53 * mm});
            skCircle(sketch, "E213", {"center": v(14560.55, 5092.7) * mm, "radius": 9.53 * mm});
            skCircle(sketch, "E214", {"center": v(14560.55, 8140.7) * mm, "radius": 9.53 * mm});
            skCircle(sketch, "E215", {"center": v(14376.4, 8464.55) * mm, "radius": 9.53 * mm});
            skLineSegment(sketch, "E216", {"start": v(12331.7, 8464.55) * mm, "end": v(12585.7, 8464.55) * mm, "construction": true});
            skLineSegment(sketch, "E217", {"start": v(12331.7, 8464.55) * mm, "end": v(12077.7, 8464.55) * mm, "construction": true});
            skCircle(sketch, "E218", {"center": v(12585.7, 8464.55) * mm, "radius": 9.53 * mm});
            skCircle(sketch, "E219", {"center": v(12077.7, 8464.55) * mm, "radius": 9.53 * mm});
            skCircle(sketch, "E220", {"center": v(9537.7, 8464.55) * mm, "radius": 9.53 * mm});
            skCircle(sketch, "E221", {"center": v(9029.7, 8464.55) * mm, "radius": 9.53 * mm});
            skCircle(sketch, "E222", {"center": v(6489.7, 8464.55) * mm, "radius": 9.53 * mm});
            skCircle(sketch, "E223", {"center": v(5981.7, 8464.55) * mm, "radius": 9.53 * mm});
            skCircle(sketch, "E224", {"center": v(3441.7, 8464.55) * mm, "radius": 9.53 * mm});
            skCircle(sketch, "E225", {"center": v(2933.7, 8464.55) * mm, "radius": 9.53 * mm});
            skCircle(sketch, "E226", {"center": v(393.7, 8464.55) * mm, "radius": 9.53 * mm});
            skSolve(sketch);
        }
        {
            var Q0;
            Q0=makeQuery(id+"F31.imprint","IMPRINT",FACE,{"disambiguationData":[TD([[makeQuery(id+"F31.imprint","IMPRINT",EDGE,{"derivedFrom":sQuery(id+"F31.wireOp",EDGE,"E145")}),1.0]])]});
            var Q1;
            Q1=makeQuery(id+"F31.imprint","IMPRINT",FACE,{"disambiguationData":[TD([[makeQuery(id+"F31.imprint","IMPRINT",EDGE,{"derivedFrom":sQuery(id+"F31.wireOp",EDGE,"E148")}),1.0]])]});
            var Q2;
            Q2=makeQuery(id+"F31.imprint","IMPRINT",FACE,{"disambiguationData":[TD([[makeQuery(id+"F31.imprint","IMPRINT",EDGE,{"derivedFrom":sQuery(id+"F31.wireOp",EDGE,"E150")}),1.0]])]});
            var Q3;
            Q3=makeQuery(id+"F31.imprint","IMPRINT",FACE,{"disambiguationData":[TD([[makeQuery(id+"F31.imprint","IMPRINT",EDGE,{"derivedFrom":sQuery(id+"F31.wireOp",EDGE,"E155")}),1.0]])]});
            var Q4;
            Q4=makeQuery(id+"F31.imprint","IMPRINT",FACE,{"disambiguationData":[TD([[makeQuery(id+"F31.imprint","IMPRINT",EDGE,{"derivedFrom":sQuery(id+"F31.wireOp",EDGE,"E156")}),1.0]])]});
            var Q5;
            Q5=makeQuery(id+"F31.imprint","IMPRINT",FACE,{"disambiguationData":[TD([[makeQuery(id+"F31.imprint","IMPRINT",EDGE,{"derivedFrom":sQuery(id+"F31.wireOp",EDGE,"E158")}),1.0]])]});
            var Q6;
            Q6=makeQuery(id+"F31.imprint","IMPRINT",FACE,{"disambiguationData":[TD([[makeQuery(id+"F31.imprint","IMPRINT",EDGE,{"derivedFrom":sQuery(id+"F31.wireOp",EDGE,"E199")}),1.0]])]});
            var Q7;
            Q7=makeQuery(id+"F31.imprint","IMPRINT",FACE,{"disambiguationData":[TD([[makeQuery(id+"F31.imprint","IMPRINT",EDGE,{"derivedFrom":sQuery(id+"F31.wireOp",EDGE,"E200")}),1.0]])]});
            var Q8;
            Q8=makeQuery(id+"F31.imprint","IMPRINT",FACE,{"disambiguationData":[TD([[makeQuery(id+"F31.imprint","IMPRINT",EDGE,{"derivedFrom":sQuery(id+"F31.wireOp",EDGE,"E201")}),1.0]])]});
            var Q9;
            Q9=makeQuery(id+"F31.imprint","IMPRINT",FACE,{"disambiguationData":[TD([[makeQuery(id+"F31.imprint","IMPRINT",EDGE,{"derivedFrom":sQuery(id+"F31.wireOp",EDGE,"E202")}),1.0]])]});
            var Q10;
            Q10=makeQuery(id+"F31.imprint","IMPRINT",FACE,{"disambiguationData":[TD([[makeQuery(id+"F31.imprint","IMPRINT",EDGE,{"derivedFrom":sQuery(id+"F31.wireOp",EDGE,"E203")}),1.0]])]});
            var Q11;
            Q11=makeQuery(id+"F31.imprint","IMPRINT",FACE,{"disambiguationData":[TD([[makeQuery(id+"F31.imprint","IMPRINT",EDGE,{"derivedFrom":sQuery(id+"F31.wireOp",EDGE,"E204")}),1.0]])]});
            var Q12;
            Q12=makeQuery(id+"F31.imprint","IMPRINT",FACE,{"disambiguationData":[TD([[makeQuery(id+"F31.imprint","IMPRINT",EDGE,{"derivedFrom":sQuery(id+"F31.wireOp",EDGE,"E205")}),1.0]])]});
            var Q13;
            Q13=makeQuery(id+"F31.imprint","IMPRINT",FACE,{"disambiguationData":[TD([[makeQuery(id+"F31.imprint","IMPRINT",EDGE,{"derivedFrom":sQuery(id+"F31.wireOp",EDGE,"E206")}),1.0]])]});
            var Q14;
            Q14=makeQuery(id+"F31.imprint","IMPRINT",FACE,{"disambiguationData":[TD([[makeQuery(id+"F31.imprint","IMPRINT",EDGE,{"derivedFrom":sQuery(id+"F31.wireOp",EDGE,"E207")}),1.0]])]});
            var Q15;
            Q15=makeQuery(id+"F31.imprint","IMPRINT",FACE,{"disambiguationData":[TD([[makeQuery(id+"F31.imprint","IMPRINT",EDGE,{"derivedFrom":sQuery(id+"F31.wireOp",EDGE,"E208")}),1.0]])]});
            var Q16;
            Q16=makeQuery(id+"F31.imprint","IMPRINT",FACE,{"disambiguationData":[TD([[makeQuery(id+"F31.imprint","IMPRINT",EDGE,{"derivedFrom":sQuery(id+"F31.wireOp",EDGE,"E209")}),1.0]])]});
            var Q17;
            Q17=makeQuery(id+"F31.imprint","IMPRINT",FACE,{"disambiguationData":[TD([[makeQuery(id+"F31.imprint","IMPRINT",EDGE,{"derivedFrom":sQuery(id+"F31.wireOp",EDGE,"E210")}),1.0]])]});
            var Q18;
            Q18=makeQuery(id+"F31.imprint","IMPRINT",FACE,{"disambiguationData":[TD([[makeQuery(id+"F31.imprint","IMPRINT",EDGE,{"derivedFrom":sQuery(id+"F31.wireOp",EDGE,"E211")}),1.0]])]});
            var Q19;
            Q19=makeQuery(id+"F31.imprint","IMPRINT",FACE,{"disambiguationData":[TD([[makeQuery(id+"F31.imprint","IMPRINT",EDGE,{"derivedFrom":sQuery(id+"F31.wireOp",EDGE,"E213")}),1.0]])]});
            var Q20;
            Q20=makeQuery(id+"F31.imprint","IMPRINT",FACE,{"disambiguationData":[TD([[makeQuery(id+"F31.imprint","IMPRINT",EDGE,{"derivedFrom":sQuery(id+"F31.wireOp",EDGE,"E212")}),1.0]])]});
            var Q21;
            Q21=makeQuery(id+"F31.imprint","IMPRINT",FACE,{"disambiguationData":[TD([[makeQuery(id+"F31.imprint","IMPRINT",EDGE,{"derivedFrom":sQuery(id+"F31.wireOp",EDGE,"E214")}),1.0]])]});
            var Q22;
            Q22=makeQuery(id+"F31.imprint","IMPRINT",FACE,{"disambiguationData":[TD([[makeQuery(id+"F31.imprint","IMPRINT",EDGE,{"derivedFrom":sQuery(id+"F31.wireOp",EDGE,"E215")}),1.0]])]});
            var Q23;
            Q23=makeQuery(id+"F31.imprint","IMPRINT",FACE,{"disambiguationData":[TD([[makeQuery(id+"F31.imprint","IMPRINT",EDGE,{"derivedFrom":sQuery(id+"F31.wireOp",EDGE,"E218")}),1.0]])]});
            var Q24;
            Q24=makeQuery(id+"F31.imprint","IMPRINT",FACE,{"disambiguationData":[TD([[makeQuery(id+"F31.imprint","IMPRINT",EDGE,{"derivedFrom":sQuery(id+"F31.wireOp",EDGE,"E219")}),1.0]])]});
            var Q25;
            Q25=makeQuery(id+"F31.imprint","IMPRINT",FACE,{"disambiguationData":[TD([[makeQuery(id+"F31.imprint","IMPRINT",EDGE,{"derivedFrom":sQuery(id+"F31.wireOp",EDGE,"E220")}),1.0]])]});
            var Q26;
            Q26=makeQuery(id+"F31.imprint","IMPRINT",FACE,{"disambiguationData":[TD([[makeQuery(id+"F31.imprint","IMPRINT",EDGE,{"derivedFrom":sQuery(id+"F31.wireOp",EDGE,"E221")}),1.0]])]});
            var Q27;
            Q27=makeQuery(id+"F31.imprint","IMPRINT",FACE,{"disambiguationData":[TD([[makeQuery(id+"F31.imprint","IMPRINT",EDGE,{"derivedFrom":sQuery(id+"F31.wireOp",EDGE,"E222")}),1.0]])]});
            var Q28;
            Q28=makeQuery(id+"F31.imprint","IMPRINT",FACE,{"disambiguationData":[TD([[makeQuery(id+"F31.imprint","IMPRINT",EDGE,{"derivedFrom":sQuery(id+"F31.wireOp",EDGE,"E223")}),1.0]])]});
            var Q29;
            Q29=makeQuery(id+"F31.imprint","IMPRINT",FACE,{"disambiguationData":[TD([[makeQuery(id+"F31.imprint","IMPRINT",EDGE,{"derivedFrom":sQuery(id+"F31.wireOp",EDGE,"E224")}),1.0]])]});
            var Q30;
            Q30=makeQuery(id+"F31.imprint","IMPRINT",FACE,{"disambiguationData":[TD([[makeQuery(id+"F31.imprint","IMPRINT",EDGE,{"derivedFrom":sQuery(id+"F31.wireOp",EDGE,"E225")}),1.0]])]});
            var Q31;
            Q31=makeQuery(id+"F31.imprint","IMPRINT",FACE,{"disambiguationData":[TD([[makeQuery(id+"F31.imprint","IMPRINT",EDGE,{"derivedFrom":sQuery(id+"F31.wireOp",EDGE,"E226")}),1.0]])]});
            extrude(context, id + "F32", {"entities" : qUnion([Q0, Q1, Q2, Q3, Q4, Q5, Q6, Q7, Q8, Q9, Q10, Q11, Q12, Q13, Q14, Q15, Q16, Q17, Q18, Q19, Q20, Q21, Q22, Q23, Q24, Q25, Q26, Q27, Q28, Q29, Q30, Q31]), "operationType" : NewBodyOperationType.REMOVE, "oppositeDirection" : true, "depth" : 101.6 * mm});
        }
    });
